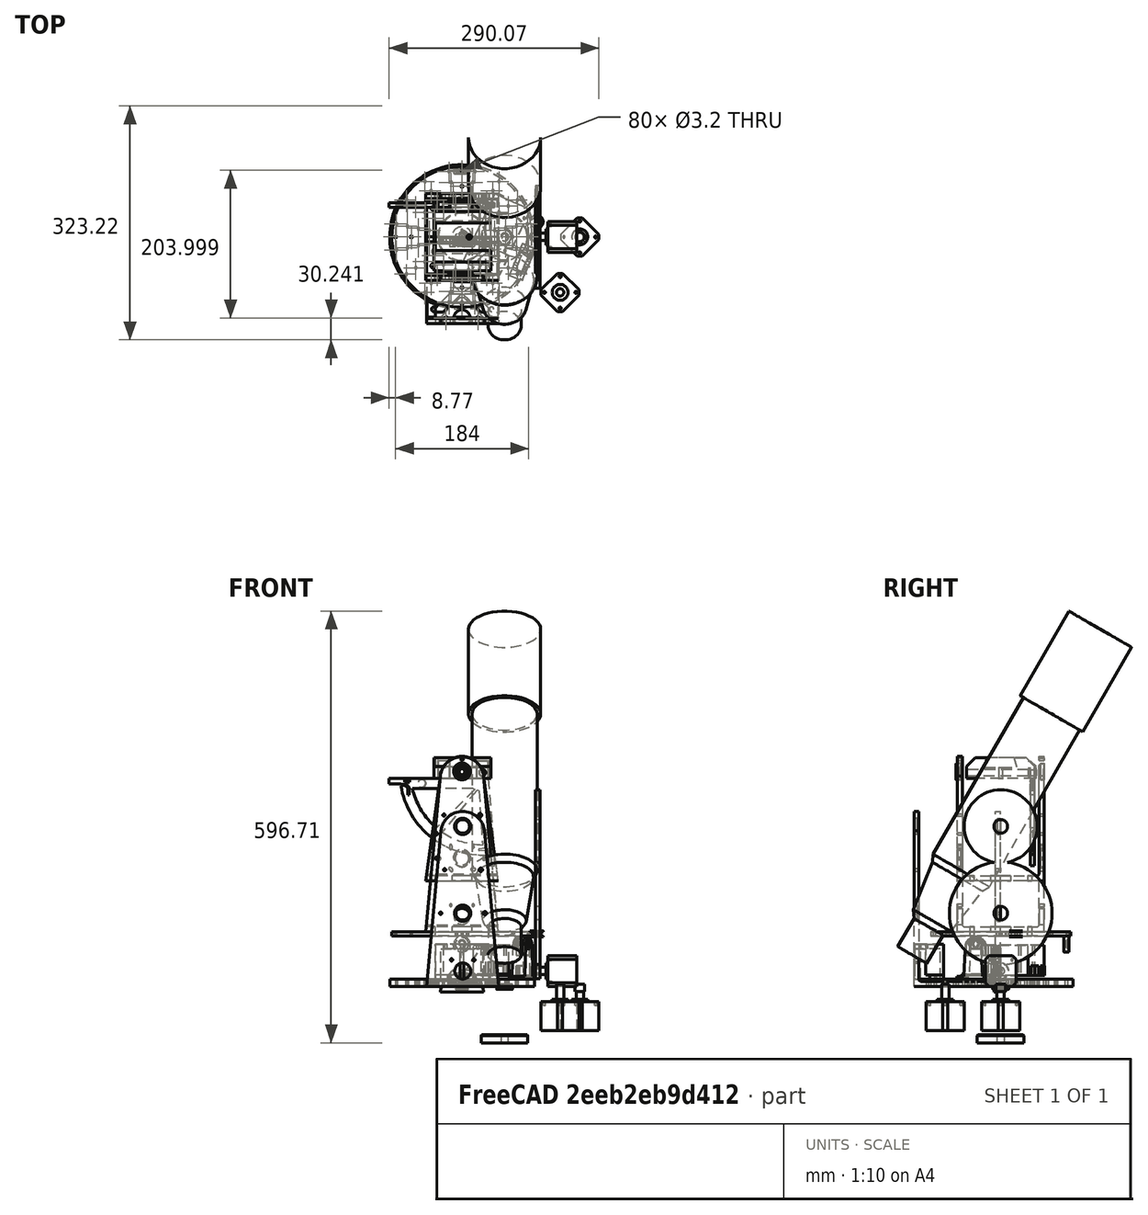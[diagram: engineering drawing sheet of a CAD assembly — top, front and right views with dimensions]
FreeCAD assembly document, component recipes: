
FREECAD ASSEMBLY — COMPONENT RECIPES ("202207 BATS - Begines Astro Tracking System")

This assembly document has 31 components, labeled P0..P30 below (a component is one placed body or linked part). 31 of them carry a construction recipe — the FreeCAD feature program that regenerates the part from scratch, quoted from this document or its linked companion documents; the rest are supplied as boundary geometry only. No exploded tour is included for this assembly.
NOTE — this tour is split across 2 documents so each fits a 32k-token context. This is document 1: the component sections continue in the remaining 1 document, each repeating the header above.
COMPONENT P0 — recipe-attached ("TRIPODE", modeled in this document).
Construction recipe (the document's own serialized feature program — sketch geometry with constraints, then the solid features built on it; lengths are millimeters unless a unit is written):

FEATURE [Sketcher::SketchObject] Sketch
  FullyConstrained = true
  MapMode = 5
  Support = -> [XY_Plane]
  sketch-geometry (2):
    g0: Circle CenterX=0 CenterY=0 CenterZ=0 NormalX=0 NormalY=0 NormalZ=1 AngleXU=0 Radius=32.25
    g1: Circle CenterX=0 CenterY=0 CenterZ=0 NormalX=0 NormalY=0 NormalZ=1 AngleXU=0 Radius=5.15
  constraints (4):
    c: Coincident(g0,g-1)
    c: Radius(g0) = 32.25
    c: Coincident(g1,g0)
    c: Radius(g1) = 5.15
FEATURE [PartDesign::Pad] Pad
  Direction = (1,1,1)
  Length = 11
  Length2 = 100
  Profile = -> Sketch
  Type = 0
FEATURE [PartDesign::Chamfer] Chamfer004
  Angle = 45
  Base = -> Pad [Edge3]
  BaseFeature = -> Pad
  ChamferType = 0
  FlipDirection = false
  Size = 1
  Size2 = 1
  SupportTransform = false
FEATURE [PartDesign::Body] Body  label="TRIPODE"
  Group = -> [Sketch,Pad,Chamfer004]
  Origin = -> Origin
  Placement = pos=(58.8,-0.2,-78) rot=(0,0,1;0rad)
  Tip = -> Chamfer004
COMPONENT P1 — recipe-attached ("BASE", modeled in this document).
Construction recipe (the document's own serialized feature program — sketch geometry with constraints, then the solid features built on it; lengths are millimeters unless a unit is written):

FEATURE [Sketcher::SketchObject] Sketch006
  FullyConstrained = true
  MapMode = 5
  Support = -> [XY_Plane002]
  sketch-geometry (17):
    g0: Circle CenterX=0 CenterY=0 CenterZ=0 NormalX=0 NormalY=0 NormalZ=1 AngleXU=0 Radius=97.1
    g1: Circle CenterX=0 CenterY=0 CenterZ=0 NormalX=0 NormalY=0 NormalZ=1 AngleXU=0 Radius=6.35
    g2: Circle CenterX=-40 CenterY=40 CenterZ=0 NormalX=0 NormalY=0 NormalZ=1 AngleXU=0 Radius=3.15
    g3: Circle CenterX=40 CenterY=40 CenterZ=0 NormalX=0 NormalY=0 NormalZ=1 AngleXU=0 Radius=3.15
    g4: Circle CenterX=40 CenterY=-40 CenterZ=0 NormalX=0 NormalY=0 NormalZ=1 AngleXU=0 Radius=3.15
    g5: Circle CenterX=-40 CenterY=-40 CenterZ=0 NormalX=0 NormalY=0 NormalZ=1 AngleXU=0 Radius=3.15
    g6: Circle CenterX=0 CenterY=92 CenterZ=0 NormalX=0 NormalY=0 NormalZ=1 AngleXU=0 Radius=1.6
    g7: Circle CenterX=0 CenterY=70 CenterZ=0 NormalX=0 NormalY=0 NormalZ=1 AngleXU=0 Radius=1.6
    g8: Circle CenterX=70 CenterY=0 CenterZ=0 NormalX=0 NormalY=0 NormalZ=1 AngleXU=0 Radius=1.6
    g9: Circle CenterX=92 CenterY=0 CenterZ=0 NormalX=0 NormalY=0 NormalZ=1 AngleXU=0 Radius=1.6
    g10: Circle CenterX=0 CenterY=-70 CenterZ=0 NormalX=0 NormalY=0 NormalZ=1 AngleXU=0 Radius=1.6
    g11: Circle CenterX=0 CenterY=-92 CenterZ=0 NormalX=0 NormalY=0 NormalZ=1 AngleXU=0 Radius=1.6
    g12: Circle CenterX=-92 CenterY=0 CenterZ=0 NormalX=0 NormalY=0 NormalZ=1 AngleXU=0 Radius=1.6
    g13: Circle CenterX=-70 CenterY=0 CenterZ=0 NormalX=0 NormalY=0 NormalZ=1 AngleXU=0 Radius=1.6
    g14: Circle CenterX=0 CenterY=9 CenterZ=0 NormalX=0 NormalY=0 NormalZ=1 AngleXU=0 Radius=1.55
    g15: Circle CenterX=7.79423 CenterY=-4.5 CenterZ=0 NormalX=0 NormalY=0 NormalZ=1 AngleXU=0 Radius=1.55
    g16: Circle CenterX=-7.79423 CenterY=-4.5 CenterZ=0 NormalX=0 NormalY=0 NormalZ=1 AngleXU=0 Radius=1.55
  constraints (48):
    c: Coincident(g0,g-1)
    c: Radius(g0) = 97.1
    c: Coincident(g1,g0)
    c: Equal(g2,g3)
    c: Equal(g2,g4)
    c: Equal(g2,g5)
    c: Radius(g2) = 3.15
    c: Horizontal(g2,g3)
    c: Horizontal(g5,g4)
    c: Vertical(g2,g5)
    c: DistanceX(g2,g3) = 80
    c: Vertical(g3,g4)
    c: DistanceY(g5,g2) = 80
    c: Symmetric(g2,g4,g0)
    c: PointOnObject(g6,g-2)
    c: PointOnObject(g7,g-2)
    c: PointOnObject(g8,g-1)
    c: PointOnObject(g9,g-1)
    c: PointOnObject(g10,g-2)
    c: PointOnObject(g11,g-2)
    c: PointOnObject(g12,g-1)
    c: PointOnObject(g13,g-1)
    c: Equal(g9,g8)
    c: Equal(g9,g10)
    c: Equal(g9,g11)
    c: Equal(g9,g13)
    c: Equal(g9,g12)
    c: Equal(g9,g7)
    c: Equal(g9,g6)
    c: Radius(g9) = 1.6
    c: DistanceX(g12,g0) = 92
    c: DistanceX(g9) = 92
    c: DistanceY(g6) = 92
    c: DistanceY(g11) = -92
    c: DistanceY(g10) = -70
    c: DistanceX(g8) = 70
    c: DistanceX(g13) = -70
    c: DistanceY(g7) = 70
    c: Radius(g1) = 6.35
    c: PointOnObject(g14,g-2)
    c: Equal(g14,g16)
    c: Equal(g14,g15)
    c: Radius(g14) = 1.55
    c: Distance(g14,g0) = 9
    c: Distance(g0,g15) = 9
    c: Symmetric(g16,g15,g-2)
    c: Distance(g14,g16) = 15.5885
    c: Distance(g16,g15) = 15.5885
FEATURE [PartDesign::Pad] Pad002
  Direction = (1,1,1)
  Length = 6
  Length2 = 100
  Profile = -> Sketch006
  Type = 0
FEATURE [PartDesign::Chamfer] Chamfer
  Angle = 45
  Base = -> Pad002 [Edge5,Edge6]
  BaseFeature = -> Pad002
  ChamferType = 0
  FlipDirection = false
  Size = 0.4
  Size2 = 1
  SupportTransform = false
FEATURE [PartDesign::Body] Body002  label="BASE"
  Group = -> [Sketch006,Pad002,Chamfer]
  Origin = -> Origin002
  Placement = pos=(-6e-15,0,69.6) rot=(0,0,1;0rad)
  Tip = -> Chamfer
COMPONENT P2 — recipe-attached ("BEARING 22x8x7base", modeled in this document).
Construction recipe (the document's own serialized feature program — sketch geometry with constraints, then the solid features built on it; lengths are millimeters unless a unit is written):

FEATURE [Sketcher::SketchObject] Sketch009
  FullyConstrained = true
  MapMode = 5
  Support = -> [XY_Plane003]
  sketch-geometry (2):
    g0: Circle CenterX=0 CenterY=0 CenterZ=0 NormalX=0 NormalY=0 NormalZ=1 AngleXU=0 Radius=4
    g1: Circle CenterX=0 CenterY=0 CenterZ=0 NormalX=0 NormalY=0 NormalZ=1 AngleXU=0 Radius=11
  constraints (4):
    c: Coincident(g0,g-1)
    c: Coincident(g1,g0)
    c: Radius(g0) = 4
    c: Radius(g1) = 11
FEATURE [PartDesign::Pad] Pad003
  Direction = (1,1,1)
  Length = 7
  Length2 = 100
  Profile = -> Sketch009
  Type = 0
FEATURE [Sketcher::SketchObject] Sketch011
  FullyConstrained = true
  MapMode = 5
  Placement = pos=(0,0,7) rot=(0,0,1;0rad)
  Support = -> [Pad003]
  sketch-geometry (2):
    g0: Circle CenterX=0 CenterY=0 CenterZ=0 NormalX=0 NormalY=0 NormalZ=1 AngleXU=0 Radius=5.5
    g1: Circle CenterX=0 CenterY=0 CenterZ=0 NormalX=0 NormalY=0 NormalZ=1 AngleXU=0 Radius=5.6
  constraints (4):
    c: Coincident(g0,g-1)
    c: Coincident(g1,g0)
    c: Radius(g0) = 5.5
    c: Radius(g1) = 5.6
FEATURE [PartDesign::Pocket] Pocket004
  BaseFeature = -> Pad003
  Length = 3
  Length2 = 100
  Midplane = true
  Profile = -> Sketch011
  Reversed = true
  Type = 0
FEATURE [Sketcher::SketchObject] Sketch010
  FullyConstrained = true
  MapMode = 5
  Placement = pos=(0,0,0) rot=(1,0,0;3.14159rad)
  Support = -> [Pocket004]
  sketch-geometry (2):
    g0: Circle CenterX=0 CenterY=0 CenterZ=0 NormalX=0 NormalY=0 NormalZ=1 AngleXU=0 Radius=5.5
    g1: Circle CenterX=0 CenterY=0 CenterZ=0 NormalX=0 NormalY=0 NormalZ=1 AngleXU=0 Radius=5.6
  constraints (4):
    c: Coincident(g0,g-1)
    c: Coincident(g1,g0)
    c: Radius(g0) = 5.5
    c: Radius(g1) = 5.6
FEATURE [PartDesign::Pocket] Pocket007
  BaseFeature = -> Pocket004
  Length = 3
  Length2 = 100
  Profile = -> Sketch010
  Type = 0
FEATURE [Sketcher::SketchObject] Sketch008
  FullyConstrained = true
  MapMode = 5
  Placement = pos=(0,0,7) rot=(0,0,1;0rad)
  Support = -> [Pocket007]
  sketch-geometry (2):
    g0: Circle CenterX=0 CenterY=0 CenterZ=0 NormalX=0 NormalY=0 NormalZ=1 AngleXU=0 Radius=9
    g1: Circle CenterX=0 CenterY=0 CenterZ=0 NormalX=0 NormalY=0 NormalZ=1 AngleXU=0 Radius=9.1
  constraints (4):
    c: Coincident(g0,g-1)
    c: Coincident(g1,g0)
    c: Radius(g0) = 9
    c: Radius(g1) = 9.1
FEATURE [PartDesign::Pocket] Pocket006
  BaseFeature = -> Pocket007
  Length = 1
  Length2 = 100
  Profile = -> Sketch008
  Type = 0
FEATURE [Sketcher::SketchObject] Sketch007
  FullyConstrained = true
  MapMode = 5
  Placement = pos=(0,0,0) rot=(1,0,0;3.14159rad)
  Support = -> [Pocket006]
  sketch-geometry (2):
    g0: Circle CenterX=0 CenterY=0 CenterZ=0 NormalX=0 NormalY=0 NormalZ=1 AngleXU=0 Radius=9
    g1: Circle CenterX=0 CenterY=0 CenterZ=0 NormalX=0 NormalY=0 NormalZ=1 AngleXU=0 Radius=9.1
  constraints (4):
    c: Coincident(g0,g-1)
    c: Coincident(g1,g0)
    c: Radius(g0) = 9
    c: Radius(g1) = 9.1
FEATURE [PartDesign::Pocket] Pocket005
  BaseFeature = -> Pocket006
  Length = 1
  Length2 = 100
  Profile = -> Sketch007
  Type = 0
FEATURE [PartDesign::Fillet] Fillet001
  Base = -> Pocket005 [Edge2,Edge3]
  BaseFeature = -> Pocket005
  Radius = 0.2
  SupportTransform = false
FEATURE [PartDesign::Body] Body003  label="BEARING 22x8x7base"
  Group = -> [Sketch009,Pad003,Sketch011,Pocket004,Sketch010,Pocket007,Sketch008,Pocket006,Sketch007,Pocket005,Fillet001]
  Origin = -> Origin003
  Placement = pos=(59,0,-4) rot=(0,0,1;0rad)
  Tip = -> Fillet001
COMPONENT P3 — recipe-attached ("GEARS", modeled in this document).
Construction recipe (the document's own serialized feature program — sketch geometry with constraints, then the solid features built on it; lengths are millimeters unless a unit is written):

FEATURE [Sketcher::SketchObject] Sketch017
  FullyConstrained = true
  MapMode = 5
  Placement = pos=(0,0,0) rot=(0.57735,0.57735,0.57735;2.0944rad)
  Support = -> [YZ_Plane004]
  sketch-geometry (7):
    g0: ArcOfCircle CenterX=0 CenterY=221.15 CenterZ=0 NormalX=0 NormalY=0 NormalZ=1 AngleXU=0 Radius=50.5 StartAngle=4.89915 EndAngle=10.8088
    g1: ArcOfCircle CenterX=0 CenterY=21.15 CenterZ=0 NormalX=0 NormalY=0 NormalZ=1 AngleXU=0 Radius=10.5 StartAngle=2.07708 EndAngle=7.3477
    g2: ArcOfCircle CenterX=0 CenterY=101.15 CenterZ=0 NormalX=0 NormalY=0 NormalZ=1 AngleXU=0 Radius=71 StartAngle=4.78417 EndAngle=7.72153
    g3: ArcOfCircle CenterX=0 CenterY=101.15 CenterZ=0 NormalX=0 NormalY=0 NormalZ=1 AngleXU=0 Radius=71 StartAngle=1.70325 EndAngle=4.64061
    g4: Circle CenterX=0 CenterY=101.15 CenterZ=0 NormalX=0 NormalY=0 NormalZ=1 AngleXU=0 Radius=9.5
    g5: Circle CenterX=0 CenterY=221.15 CenterZ=0 NormalX=0 NormalY=0 NormalZ=1 AngleXU=0 Radius=9.5
    g6: Circle CenterX=0 CenterY=21.15 CenterZ=0 NormalX=0 NormalY=0 NormalZ=1 AngleXU=0 Radius=2.6
  constraints (21):
    c: Radius(g0) = 50.5
    c: Radius(g1) = 10.5
    c: Coincident(g2,g0)
    c: Coincident(g2,g1)
    c: Coincident(g3,g2)
    c: Coincident(g3,g0)
    c: Coincident(g3,g1)
    c: DistanceY(g0) = 221.15
    c: DistanceY(g2) = 101.15
    c: Radius(g2) = 71
    c: Radius(g3) = 71
    c: Coincident(g4,g2)
    c: Coincident(g5,g0)
    c: Radius(g4) = 9.5
    c: Radius(g5) = 9.5
    c: Coincident(g6,g1)
    c: Radius(g6) = 2.6
    c: DistanceY(g1) = 21.15
    c: PointOnObject(g1,g-2)
    c: PointOnObject(g2,g-2)
    c: PointOnObject(g0,g-2)
FEATURE [PartDesign::Pad] Pad011
  Direction = (1,1,1)
  Length = 6
  Length2 = 100
  Placement = pos=(0,0,0) rot=(0.57735,0.57735,0.57735;2.0944rad)
  Profile = -> Sketch017
  Type = 0
FEATURE [PartDesign::Body] Body004  label="GEARS"
  Group = -> [Sketch017,Pad011]
  Origin = -> Origin004
  Placement = pos=(101.8,0,0) rot=(0,0,1;0rad)
  Tip = -> Pad011
COMPONENT P4 — recipe-attached ("TELESCOPIO", modeled in this document).
Construction recipe (the document's own serialized feature program — sketch geometry with constraints, then the solid features built on it; lengths are millimeters unless a unit is written):

FEATURE [Sketcher::SketchObject] Sketch014
  FullyConstrained = true
  MapMode = 5
  Support = -> [XY_Plane005]
  sketch-geometry (10):
    g0: LineSegment StartX=0 StartY=0 StartZ=0 EndX=0 EndY=50 EndZ=0
    g1: LineSegment StartX=0 StartY=50 StartZ=0 EndX=135 EndY=50 EndZ=0
    g2: LineSegment StartX=135 StartY=50 StartZ=0 EndX=135 EndY=45 EndZ=0
    g3: LineSegment StartX=135 StartY=45 StartZ=0 EndX=385 EndY=45 EndZ=0
    g4: LineSegment StartX=385 StartY=45 StartZ=0 EndX=395 EndY=40 EndZ=0
    g5: LineSegment StartX=395 StartY=40 StartZ=0 EndX=465 EndY=30 EndZ=0
    g6: LineSegment StartX=465 StartY=30 StartZ=0 EndX=475 EndY=23 EndZ=0
    g7: LineSegment StartX=520 StartY=0 StartZ=0 EndX=0 EndY=0 EndZ=0
    g8: LineSegment StartX=475 StartY=23 StartZ=0 EndX=520 EndY=23 EndZ=0
    g9: LineSegment StartX=520 StartY=23 StartZ=0 EndX=520 EndY=0 EndZ=0
  constraints (29):
    c: Coincident(g0,g1)
    c: Horizontal(g1)
    c: Coincident(g1,g2)
    c: Coincident(g2,g3)
    c: Horizontal(g3)
    c: Coincident(g3,g4)
    c: Coincident(g4,g5)
    c: Coincident(g5,g6)
    c: Coincident(g7,g0)
    c: Horizontal(g7)
    c: Vertical(g0)
    c: DistanceY(g0,g0) = 50
    c: Vertical(g2)
    c: DistanceY(g0,g2) = 45
    c: DistanceX(g1,g1) = 135
    c: DistanceX(g3,g3) = 250
    c: DistanceX(g3,g5) = 80
    c: DistanceY(g-1,g4) = 40
    c: DistanceX(g3,g4) = 10
    c: DistanceY(g-1,g5) = 30
    c: Coincident(g6,g8)
    c: Horizontal(g8)
    c: Coincident(g8,g9)
    c: Coincident(g9,g7)
    c: DistanceY(g-1,g8) = 23
    c: DistanceX(g6,g6) = 10
    c: Vertical(g9)
    c: DistanceX(g8,g8) = 45
    c: Coincident(g-1,g0)
FEATURE [PartDesign::Revolution] Revolution
  Angle = 360
  Axis = (1,0,0)
  Base = (0,0,0)
  Profile = -> Sketch014
  ReferenceAxis = -> Sketch014 [H_Axis]
FEATURE [PartDesign::Body] Body005  label="TELESCOPIO"
  Group = -> [Sketch014,Revolution]
  Origin = -> Origin005
  Placement = pos=(58.8541,137.678,493.712) rot=(0.447214,0.447214,-0.774597;1.82348rad)
  Tip = -> Revolution
COMPONENT P5 — recipe-attached ("NEMA17", modeled in this document).
Construction recipe (the document's own serialized feature program — sketch geometry with constraints, then the solid features built on it; lengths are millimeters unless a unit is written):

FEATURE [Sketcher::SketchObject] Sketch018
  FullyConstrained = true
  MapMode = 5
  Support = -> [XY_Plane006]
  sketch-geometry (4):
    g0: LineSegment StartX=-21.15 StartY=21.15 StartZ=0 EndX=21.15 EndY=21.15 EndZ=0
    g1: LineSegment StartX=21.15 StartY=21.15 StartZ=0 EndX=21.15 EndY=-21.15 EndZ=0
    g2: LineSegment StartX=21.15 StartY=-21.15 StartZ=0 EndX=-21.15 EndY=-21.15 EndZ=0
    g3: LineSegment StartX=-21.15 StartY=-21.15 StartZ=0 EndX=-21.15 EndY=21.15 EndZ=0
  constraints (11):
    c: Coincident(g0,g1)
    c: Coincident(g1,g2)
    c: Coincident(g2,g3)
    c: Coincident(g3,g0)
    c: Horizontal(g0)
    c: Horizontal(g2)
    c: Vertical(g1)
    c: Vertical(g3)
    c: DistanceX(g0,g0) = 42.3
    c: DistanceY(g1,g1) = 42.3
    c: Symmetric(g0,g1,g-1)
FEATURE [PartDesign::Pad] Pad005
  Direction = (1,1,1)
  Length = 40
  Length2 = 100
  Profile = -> Sketch018
  Type = 0
FEATURE [Sketcher::SketchObject] Sketch019
  FullyConstrained = true
  MapMode = 5
  Placement = pos=(0,0,40) rot=(0,0,1;0rad)
  Support = -> [Pad005]
  sketch-geometry (1):
    g0: Circle CenterX=0 CenterY=0 CenterZ=0 NormalX=0 NormalY=0 NormalZ=1 AngleXU=0 Radius=11
  constraints (2):
    c: Coincident(g0,g-1)
    c: Radius(g0) = 11
FEATURE [PartDesign::Pad] Pad006
  BaseFeature = -> Pad005
  Direction = (1,1,1)
  Length = 3
  Length2 = 100
  Profile = -> Sketch019
  Type = 0
FEATURE [Sketcher::SketchObject] Sketch020
  FullyConstrained = true
  MapMode = 5
  Placement = pos=(0,0,43) rot=(0,0,1;0rad)
  Support = -> [Pad006]
  sketch-geometry (1):
    g0: Circle CenterX=0 CenterY=0 CenterZ=0 NormalX=0 NormalY=0 NormalZ=1 AngleXU=0 Radius=5.1
  constraints (2):
    c: Coincident(g0,g-1)
    c: Radius(g0) = 5.1
FEATURE [PartDesign::Pad] Pad007
  BaseFeature = -> Pad006
  Direction = (1,1,1)
  Length = 21
  Length2 = 100
  Profile = -> Sketch020
  Type = 0
FEATURE [Sketcher::SketchObject] Sketch021
  FullyConstrained = true
  MapMode = 5
  Placement = pos=(0,0,0) rot=(1,0,0;3.14159rad)
  Support = -> [Pad007]
FEATURE [Sketcher::SketchObject] Sketch022
  ExternalGeometry = -> [Pad007]
  FullyConstrained = true
  MapMode = 5
  Placement = pos=(0,0,40) rot=(0,0,1;0rad)
  Support = -> [Pad007]
  sketch-geometry (4):
    g0: Circle CenterX=-15.5 CenterY=15.5 CenterZ=0 NormalX=0 NormalY=0 NormalZ=1 AngleXU=0 Radius=1.5
    g1: Circle CenterX=15.5 CenterY=15.5 CenterZ=0 NormalX=0 NormalY=0 NormalZ=1 AngleXU=0 Radius=1.5
    g2: Circle CenterX=15.5 CenterY=-15.5 CenterZ=0 NormalX=0 NormalY=0 NormalZ=1 AngleXU=0 Radius=1.5
    g3: Circle CenterX=-15.5 CenterY=-15.5 CenterZ=0 NormalX=0 NormalY=0 NormalZ=1 AngleXU=0 Radius=1.5
  constraints (14):
    c: Equal(g0,g1)
    c: Equal(g0,g2)
    c: Equal(g0,g3)
    c: Radius(g0) = 1.5
    c: Horizontal(g0,g1)
    c: Horizontal(g3,g2)
    c: Vertical(g0,g3)
    c: Vertical(g2,g1)
    c: DistanceX(g0,g1) = 31
    c: DistanceY(g3,g0) = 31
    c: DistanceX(g-5,g0) = 5.65
    c: DistanceY(g0,g-5) = 5.65
    c: DistanceX(g1,g-5) = 5.65
    c: DistanceY(g-6,g2) = 5.65
FEATURE [PartDesign::Pocket] Pocket011
  BaseFeature = -> Pad007
  Length = 5
  Length2 = 100
  Profile = -> Sketch022
  Type = 0
FEATURE [PartDesign::Chamfer] Chamfer001
  Angle = 45
  Base = -> Pocket011 [Edge2,Edge8,Edge1,Edge5]
  BaseFeature = -> Pocket011
  ChamferType = 0
  FlipDirection = false
  Size = 5
  Size2 = 1
  SupportTransform = false
FEATURE [PartDesign::Body] Body006  label="NEMA17"
  Group = -> [Sketch018,Pad005,Sketch019,Pad006,Sketch020,Pad007,Sketch021,Sketch022,Pocket011,Chamfer001]
  Origin = -> Origin006
  Placement = pos=(135.74,-76.6447,-61.1) rot=(0,0,-1;0.785398rad)
  Tip = -> Chamfer001
COMPONENT P6 — recipe-attached ("NEMA017-A", modeled in this document).
Construction recipe (the document's own serialized feature program — sketch geometry with constraints, then the solid features built on it; lengths are millimeters unless a unit is written):

FEATURE [Sketcher::SketchObject] Sketch026
  FullyConstrained = true
  MapMode = 5
  Support = -> [XY_Plane007]
  sketch-geometry (4):
    g0: LineSegment StartX=-21.15 StartY=21.15 StartZ=0 EndX=21.15 EndY=21.15 EndZ=0
    g1: LineSegment StartX=21.15 StartY=21.15 StartZ=0 EndX=21.15 EndY=-21.15 EndZ=0
    g2: LineSegment StartX=21.15 StartY=-21.15 StartZ=0 EndX=-21.15 EndY=-21.15 EndZ=0
    g3: LineSegment StartX=-21.15 StartY=-21.15 StartZ=0 EndX=-21.15 EndY=21.15 EndZ=0
  constraints (11):
    c: Coincident(g0,g1)
    c: Coincident(g1,g2)
    c: Coincident(g2,g3)
    c: Coincident(g3,g0)
    c: Horizontal(g0)
    c: Horizontal(g2)
    c: Vertical(g1)
    c: Vertical(g3)
    c: DistanceX(g0,g0) = 42.3
    c: DistanceY(g1,g1) = 42.3
    c: Symmetric(g0,g1,g-1)
FEATURE [PartDesign::Pad] Pad008
  Direction = (1,1,1)
  Length = 40
  Length2 = 100
  Profile = -> Sketch026
  Type = 0
FEATURE [Sketcher::SketchObject] Sketch025
  FullyConstrained = true
  MapMode = 5
  Placement = pos=(0,0,40) rot=(0,0,1;0rad)
  Support = -> [Pad008]
  sketch-geometry (1):
    g0: Circle CenterX=0 CenterY=0 CenterZ=0 NormalX=0 NormalY=0 NormalZ=1 AngleXU=0 Radius=11
  constraints (2):
    c: Coincident(g0,g-1)
    c: Radius(g0) = 11
FEATURE [PartDesign::Pad] Pad009
  BaseFeature = -> Pad008
  Direction = (1,1,1)
  Length = 3
  Length2 = 100
  Profile = -> Sketch025
  Type = 0
FEATURE [Sketcher::SketchObject] Sketch023
  FullyConstrained = true
  MapMode = 5
  Placement = pos=(0,0,43) rot=(0,0,1;0rad)
  Support = -> [Pad009]
  sketch-geometry (1):
    g0: Circle CenterX=0 CenterY=0 CenterZ=0 NormalX=0 NormalY=0 NormalZ=1 AngleXU=0 Radius=5.1
  constraints (2):
    c: Coincident(g0,g-1)
    c: Radius(g0) = 5.1
FEATURE [PartDesign::Pad] Pad010
  BaseFeature = -> Pad009
  Direction = (1,1,1)
  Length = 21
  Length2 = 100
  Profile = -> Sketch023
  Type = 0
FEATURE [Sketcher::SketchObject] Sketch024
  FullyConstrained = true
  MapMode = 5
  Placement = pos=(0,0,0) rot=(1,0,0;3.14159rad)
  Support = -> [Pad010]
FEATURE [Sketcher::SketchObject] Sketch027
  ExternalGeometry = -> [Pad010]
  FullyConstrained = true
  MapMode = 5
  Placement = pos=(0,0,40) rot=(0,0,1;0rad)
  Support = -> [Pad010]
  sketch-geometry (4):
    g0: Circle CenterX=-15.5 CenterY=15.5 CenterZ=0 NormalX=0 NormalY=0 NormalZ=1 AngleXU=0 Radius=1.5
    g1: Circle CenterX=15.5 CenterY=15.5 CenterZ=0 NormalX=0 NormalY=0 NormalZ=1 AngleXU=0 Radius=1.5
    g2: Circle CenterX=15.5 CenterY=-15.5 CenterZ=0 NormalX=0 NormalY=0 NormalZ=1 AngleXU=0 Radius=1.5
    g3: Circle CenterX=-15.5 CenterY=-15.5 CenterZ=0 NormalX=0 NormalY=0 NormalZ=1 AngleXU=0 Radius=1.5
  constraints (14):
    c: Equal(g0,g1)
    c: Equal(g0,g2)
    c: Equal(g0,g3)
    c: Radius(g0) = 1.5
    c: Horizontal(g0,g1)
    c: Horizontal(g3,g2)
    c: Vertical(g0,g3)
    c: Vertical(g2,g1)
    c: DistanceX(g0,g1) = 31
    c: DistanceY(g3,g0) = 31
    c: DistanceX(g-5,g0) = 5.65
    c: DistanceY(g0,g-5) = 5.65
    c: DistanceX(g1,g-5) = 5.65
    c: DistanceY(g-6,g2) = 5.65
FEATURE [PartDesign::Pocket] Pocket012
  BaseFeature = -> Pad010
  Length = 5
  Length2 = 100
  Profile = -> Sketch027
  Type = 0
FEATURE [PartDesign::Chamfer] Chamfer002
  Angle = 45
  Base = -> Pocket012 [Edge2,Edge8,Edge1,Edge5]
  BaseFeature = -> Pocket012
  ChamferType = 0
  FlipDirection = false
  Size = 5
  Size2 = 1
  SupportTransform = false
FEATURE [PartDesign::Body] Body007  label="NEMA017-A"
  Group = -> [Sketch026,Pad008,Sketch025,Pad009,Sketch023,Pad010,Sketch024,Sketch027,Pocket012,Chamfer002]
  Origin = -> Origin007
  Placement = pos=(159,0.1,21.25) rot=(0,-1,0;1.5708rad)
  Tip = -> Chamfer002
COMPONENT P7 — recipe-attached ("MEGA", modeled in this document).
Construction recipe (the document's own serialized feature program — sketch geometry with constraints, then the solid features built on it; lengths are millimeters unless a unit is written):

FEATURE [Sketcher::SketchObject] Sketch056
  FullyConstrained = true
  MapMode = 5
  Support = -> [XY_Plane013]
  sketch-geometry (17):
    g0: LineSegment StartX=-101.6 StartY=53.34 StartZ=0 EndX=-2.54 EndY=53.34 EndZ=0
    g1: LineSegment StartX=-2.54 StartY=53.34 StartZ=0 EndX=0 EndY=50.8 EndZ=0
    g2: LineSegment StartX=0 StartY=50.8 StartZ=0 EndX=0 EndY=40.64 EndZ=0
    g3: LineSegment StartX=0 StartY=40.64 StartZ=0 EndX=2.54 EndY=38.1 EndZ=0
    g4: LineSegment StartX=2.54 StartY=38.1 StartZ=0 EndX=2.54 EndY=3.81 EndZ=0
    g5: LineSegment StartX=2.54 StartY=3.81 StartZ=0 EndX=2.84e-14 EndY=1.27 EndZ=0
    g6: LineSegment StartX=2.84e-14 StartY=1.27 StartZ=0 EndX=2.84e-14 EndY=0 EndZ=0
    g7: LineSegment StartX=2.84e-14 StartY=0 StartZ=0 EndX=-101.6 EndY=0 EndZ=0
    g8: LineSegment StartX=-101.6 StartY=0 StartZ=0 EndX=-101.6 EndY=3.175 EndZ=0
    g9: LineSegment StartX=-101.6 StartY=3.175 StartZ=0 EndX=-103.505 EndY=3.175 EndZ=0
    g10: LineSegment StartX=-103.505 StartY=3.175 StartZ=0 EndX=-103.505 EndY=12.065 EndZ=0
    g11: LineSegment StartX=-103.505 StartY=12.065 StartZ=0 EndX=-101.6 EndY=12.065 EndZ=0
    g12: LineSegment StartX=-101.6 StartY=12.065 StartZ=0 EndX=-101.6 EndY=32.385 EndZ=0
    g13: LineSegment StartX=-101.6 StartY=32.385 StartZ=0 EndX=-107.95 EndY=32.385 EndZ=0
    g14: LineSegment StartX=-107.95 StartY=32.385 StartZ=0 EndX=-107.95 EndY=43.815 EndZ=0
    g15: LineSegment StartX=-107.95 StartY=43.815 StartZ=0 EndX=-101.6 EndY=43.815 EndZ=0
    g16: LineSegment StartX=-101.6 StartY=43.815 StartZ=0 EndX=-101.6 EndY=53.34 EndZ=0
  constraints (53):
    c: Horizontal(g0)
    c: Coincident(g0,g1)
    c: Coincident(g1,g2)
    c: Vertical(g2)
    c: Coincident(g2,g3)
    c: Coincident(g3,g4)
    c: Vertical(g4)
    c: Coincident(g4,g5)
    c: Coincident(g5,g6)
    c: Vertical(g6)
    c: Coincident(g6,g7)
    c: Horizontal(g7)
    c: Coincident(g7,g8)
    c: Vertical(g8)
    c: Coincident(g8,g9)
    c: Horizontal(g9)
    c: Coincident(g9,g10)
    c: Vertical(g10)
    c: Coincident(g10,g11)
    c: Horizontal(g11)
    c: Coincident(g11,g12)
    c: Coincident(g12,g13)
    c: Horizontal(g13)
    c: Coincident(g13,g14)
    c: Vertical(g14)
    c: Coincident(g14,g15)
    c: Horizontal(g15)
    c: Coincident(g15,g16)
    c: Coincident(g16,g0)
    c: DistanceX(g15,g15) = 6.35
    c: DistanceX(g9,g9) = 1.905
    c: Vertical(g8,g11)
    c: Vertical(g11,g12)
    c: Vertical(g12,g15)
    c: Vertical(g15,g0)
    c: DistanceX(g0,g1) = 2.54
    c: DistanceY(g1,g0) = 2.54
    c: DistanceY(g2,g2) = 10.16
    c: DistanceY(g3,g2) = 2.54
    c: DistanceX(g3,g3) = 2.54
    c: DistanceY(g5,g5) = 2.54
    c: DistanceX(g5,g5) = 2.54
    c: DistanceX(g7,g4) = 104.14
    c: DistanceY(g7,g0) = 53.34
    c: DistanceY(g8,g8) = 3.175
    c: DistanceY(g10,g10) = 8.89
    c: DistanceY(g12,g12) = 20.32
    c: DistanceY(g14,g14) = 11.43
    c: DistanceY(g16,g16) = 9.525
    c: DistanceY(g6,g6) = 1.27
    c: DistanceY(g4,g4) = 34.29
    c: PointOnObject(g6,g-1)
    c: DistanceX(g6) = 0
FEATURE [PartDesign::Pad] Pad017
  Direction = (1,1,1)
  Length = 2
  Length2 = 100
  Profile = -> Sketch056
  Type = 0
FEATURE [Sketcher::SketchObject] Sketch057
  ExternalGeometry = -> [Pad017]
  FullyConstrained = true
  MapMode = 5
  Placement = pos=(0,0,2) rot=(0,0,1;0rad)
  Support = -> [Pad017]
  sketch-geometry (4):
    g0: LineSegment StartX=-101.6 StartY=53.34 StartZ=0 EndX=-31.6 EndY=53.34 EndZ=0
    g1: LineSegment StartX=-31.6 StartY=53.34 StartZ=0 EndX=-31.6 EndY=0 EndZ=0
    g2: LineSegment StartX=-31.6 StartY=0 StartZ=0 EndX=-101.6 EndY=0 EndZ=0
    g3: LineSegment StartX=-101.6 StartY=0 StartZ=0 EndX=-101.6 EndY=53.34 EndZ=0
  constraints (11):
    c: Coincident(g0,g1)
    c: Coincident(g1,g2)
    c: Coincident(g2,g3)
    c: Coincident(g3,g0)
    c: Horizontal(g0)
    c: Horizontal(g2)
    c: Vertical(g1)
    c: Vertical(g3)
    c: Coincident(g0,g-8)
    c: PointOnObject(g1,g-9)
    c: DistanceX(g0,g0) = 70
FEATURE [PartDesign::Pad] Pad018
  BaseFeature = -> Pad017
  Direction = (1,1,1)
  Length = 40
  Length2 = 29
  Offset = 11
  Profile = -> Sketch057
  Type = 0
FEATURE [Sketcher::SketchObject] Sketch058
  ExternalGeometry = -> [Pad018]
  FullyConstrained = true
  MapMode = 5
  Placement = pos=(0,0,2) rot=(0,0,1;0rad)
  Support = -> [Pad018]
  sketch-geometry (8):
    g0: LineSegment StartX=-107.95 StartY=43.815 StartZ=0 EndX=-90.95 EndY=43.815 EndZ=0
    g1: LineSegment StartX=-90.95 StartY=43.815 StartZ=0 EndX=-90.95 EndY=32.385 EndZ=0
    g2: LineSegment StartX=-90.95 StartY=32.385 StartZ=0 EndX=-107.95 EndY=32.385 EndZ=0
    g3: LineSegment StartX=-107.95 StartY=32.385 StartZ=0 EndX=-107.95 EndY=43.815 EndZ=0
    g4: LineSegment StartX=-103.505 StartY=12.065 StartZ=0 EndX=-90.505 EndY=12.065 EndZ=0
    g5: LineSegment StartX=-90.505 StartY=12.065 StartZ=0 EndX=-90.505 EndY=3.175 EndZ=0
    g6: LineSegment StartX=-90.505 StartY=3.175 StartZ=0 EndX=-103.505 EndY=3.175 EndZ=0
    g7: LineSegment StartX=-103.505 StartY=3.175 StartZ=0 EndX=-103.505 EndY=12.065 EndZ=0
  constraints (20):
    c: Coincident(g0,g1)
    c: Coincident(g1,g2)
    c: Coincident(g2,g3)
    c: Coincident(g3,g0)
    c: Horizontal(g0)
    c: Horizontal(g2)
    c: Vertical(g1)
    c: Coincident(g0,g-3)
    c: Coincident(g-3,g2)
    c: DistanceX(g0,g0) = 17
    c: Coincident(g4,g5)
    c: Coincident(g5,g6)
    c: Coincident(g6,g7)
    c: Coincident(g7,g4)
    c: Horizontal(g4)
    c: Horizontal(g6)
    c: Vertical(g5)
    c: Coincident(g4,g-4)
    c: Coincident(g-4,g6)
    c: DistanceX(g4,g4) = 13
FEATURE [PartDesign::Pad] Pad019
  BaseFeature = -> Pad018
  Direction = (1,1,1)
  Length = 11
  Length2 = 100
  Profile = -> Sketch058
  Type = 0
FEATURE [Sketcher::SketchObject] Sketch059
  ExternalGeometry = -> [Pad019]
  FullyConstrained = true
  MapMode = 5
  Placement = pos=(0,0,0) rot=(1,0,0;3.14159rad)
  Support = -> [Pad019]
  sketch-geometry (6):
    g0: Circle CenterX=-86.36 CenterY=-2.54 CenterZ=0 NormalX=0 NormalY=0 NormalZ=1 AngleXU=0 Radius=1.5875
    g1: Circle CenterX=-11.43 CenterY=-2.54 CenterZ=0 NormalX=0 NormalY=0 NormalZ=1 AngleXU=0 Radius=1.5875
    g2: Circle CenterX=-87.63 CenterY=-50.8 CenterZ=0 NormalX=0 NormalY=0 NormalZ=1 AngleXU=0 Radius=1.5875
    g3: Circle CenterX=-5.08 CenterY=-50.8 CenterZ=0 NormalX=0 NormalY=0 NormalZ=1 AngleXU=0 Radius=1.5875
    g4: Circle CenterX=-35.56 CenterY=-17.78 CenterZ=0 NormalX=0 NormalY=0 NormalZ=1 AngleXU=0 Radius=1.5875
    g5: Circle CenterX=-35.56 CenterY=-45.72 CenterZ=0 NormalX=0 NormalY=0 NormalZ=1 AngleXU=0 Radius=1.5875
  constraints (18):
    c: Equal(g0,g2)
    c: Equal(g0,g1)
    c: Equal(g0,g3)
    c: Radius(g0) = 1.5875
    c: Horizontal(g0,g1)
    c: DistanceX(g-3,g0) = 15.24
    c: DistanceY(g0) = -2.54
    c: DistanceX(g-3,g1) = 90.17
    c: DistanceY(g-4,g2) = 2.54
    c: Horizontal(g3,g2)
    c: DistanceX(g-4,g2) = 13.97
    c: DistanceX(g-4,g3) = 96.52
    c: Equal(g4,g5)
    c: Radius(g4) = 1.5875
    c: Vertical(g4,g5)
    c: DistanceX(g-4,g5) = 66.04
    c: DistanceY(g-4,g5) = 7.62
    c: DistanceY(g-4,g4) = 35.56
FEATURE [PartDesign::Pocket] Pocket
  BaseFeature = -> Pad019
  Length = 50
  Length2 = 100
  Profile = -> Sketch059
  Type = 0
FEATURE [PartDesign::Body] Body012  label="MEGA"
  Group = -> [Sketch056,Pad017,Sketch057,Pad018,Sketch058,Pad019,Sketch059,Pocket]
  Origin = -> Origin012
  Placement = pos=(2.75616,-32.0303,15.15) rot=(0,0,-1;2.00713rad)
  Tip = -> Pocket
COMPONENT P8 — recipe-attached ("NEMA017-coronado", modeled in this document).
Construction recipe (the document's own serialized feature program — sketch geometry with constraints, then the solid features built on it; lengths are millimeters unless a unit is written):

FEATURE [Sketcher::SketchObject] Sketch076
  FullyConstrained = true
  MapMode = 5
  Support = -> [XY_Plane018]
  sketch-geometry (4):
    g0: LineSegment StartX=-21.15 StartY=21.15 StartZ=0 EndX=21.15 EndY=21.15 EndZ=0
    g1: LineSegment StartX=21.15 StartY=21.15 StartZ=0 EndX=21.15 EndY=-21.15 EndZ=0
    g2: LineSegment StartX=21.15 StartY=-21.15 StartZ=0 EndX=-21.15 EndY=-21.15 EndZ=0
    g3: LineSegment StartX=-21.15 StartY=-21.15 StartZ=0 EndX=-21.15 EndY=21.15 EndZ=0
  constraints (11):
    c: Coincident(g0,g1)
    c: Coincident(g1,g2)
    c: Coincident(g2,g3)
    c: Coincident(g3,g0)
    c: Horizontal(g0)
    c: Horizontal(g2)
    c: Vertical(g1)
    c: Vertical(g3)
    c: DistanceX(g0,g0) = 42.3
    c: DistanceY(g1,g1) = 42.3
    c: Symmetric(g0,g1,g-1)
FEATURE [PartDesign::Pad] Pad024
  Direction = (1,1,1)
  Length = 40
  Length2 = 100
  Profile = -> Sketch076
  Type = 0
FEATURE [Sketcher::SketchObject] Sketch075
  FullyConstrained = true
  MapMode = 5
  Placement = pos=(0,0,40) rot=(0,0,1;0rad)
  Support = -> [Pad024]
  sketch-geometry (1):
    g0: Circle CenterX=0 CenterY=0 CenterZ=0 NormalX=0 NormalY=0 NormalZ=1 AngleXU=0 Radius=11
  constraints (2):
    c: Coincident(g0,g-1)
    c: Radius(g0) = 11
FEATURE [PartDesign::Pad] Pad025
  BaseFeature = -> Pad024
  Direction = (1,1,1)
  Length = 3
  Length2 = 100
  Profile = -> Sketch075
  Type = 0
FEATURE [Sketcher::SketchObject] Sketch077
  FullyConstrained = true
  MapMode = 5
  Placement = pos=(0,0,43) rot=(0,0,1;0rad)
  Support = -> [Pad025]
  sketch-geometry (1):
    g0: Circle CenterX=0 CenterY=0 CenterZ=0 NormalX=0 NormalY=0 NormalZ=1 AngleXU=0 Radius=5.1
  constraints (2):
    c: Coincident(g0,g-1)
    c: Radius(g0) = 5.1
FEATURE [PartDesign::Pad] Pad026
  BaseFeature = -> Pad025
  Direction = (1,1,1)
  Length = 21
  Length2 = 100
  Profile = -> Sketch077
  Type = 0
FEATURE [Sketcher::SketchObject] Sketch078
  FullyConstrained = true
  MapMode = 5
  Placement = pos=(0,0,0) rot=(1,0,0;3.14159rad)
  Support = -> [Pad026]
FEATURE [Sketcher::SketchObject] Sketch079
  ExternalGeometry = -> [Pad026]
  FullyConstrained = true
  MapMode = 5
  Placement = pos=(0,0,40) rot=(0,0,1;0rad)
  Support = -> [Pad026]
  sketch-geometry (4):
    g0: Circle CenterX=-15.5 CenterY=15.5 CenterZ=0 NormalX=0 NormalY=0 NormalZ=1 AngleXU=0 Radius=1.5
    g1: Circle CenterX=15.5 CenterY=15.5 CenterZ=0 NormalX=0 NormalY=0 NormalZ=1 AngleXU=0 Radius=1.5
    g2: Circle CenterX=15.5 CenterY=-15.5 CenterZ=0 NormalX=0 NormalY=0 NormalZ=1 AngleXU=0 Radius=1.5
    g3: Circle CenterX=-15.5 CenterY=-15.5 CenterZ=0 NormalX=0 NormalY=0 NormalZ=1 AngleXU=0 Radius=1.5
  constraints (14):
    c: Equal(g0,g1)
    c: Equal(g0,g2)
    c: Equal(g0,g3)
    c: Radius(g0) = 1.5
    c: Horizontal(g0,g1)
    c: Horizontal(g3,g2)
    c: Vertical(g0,g3)
    c: Vertical(g2,g1)
    c: DistanceX(g0,g1) = 31
    c: DistanceY(g3,g0) = 31
    c: DistanceX(g-5,g0) = 5.65
    c: DistanceY(g0,g-5) = 5.65
    c: DistanceX(g1,g-5) = 5.65
    c: DistanceY(g-6,g2) = 5.65
FEATURE [PartDesign::Pocket] Pocket047
  BaseFeature = -> Pad026
  Length = 5
  Length2 = 100
  Profile = -> Sketch079
  Type = 0
FEATURE [PartDesign::Chamfer] Chamfer008
  Angle = 45
  Base = -> Pocket047 [Edge2,Edge8,Edge1,Edge5]
  BaseFeature = -> Pocket047
  ChamferType = 0
  FlipDirection = false
  Size = 5
  Size2 = 1
  SupportTransform = false
FEATURE [Sketcher::SketchObject] Sketch080
  FullyConstrained = true
  MapMode = 5
  Placement = pos=(0,0,64) rot=(0,0,1;0rad)
  Support = -> [Chamfer008]
  sketch-geometry (1):
    g0: Circle CenterX=0 CenterY=0 CenterZ=0 NormalX=0 NormalY=0 NormalZ=1 AngleXU=0 Radius=6.75
  constraints (2):
    c: Coincident(g0,g-1)
    c: Radius(g0) = 6.75
FEATURE [PartDesign::Pad] Pad027
  BaseFeature = -> Chamfer008
  Direction = (1,1,1)
  Length = 10
  Length2 = 100
  Profile = -> Sketch080
  Reversed = true
  Type = 0
FEATURE [PartDesign::Body] Body017  label="NEMA017-coronado"
  Group = -> [Sketch076,Pad024,Sketch075,Pad025,Sketch077,Pad026,Sketch078,Sketch079,Pocket047,Chamfer008,Sketch080,Pad027]
  Origin = -> Origin017
  Placement = pos=(162.924,-0.0108408,-61.1) rot=(0,0,1;0.785398rad)
  Tip = -> Pad027
COMPONENT P9 — recipe-attached ("AGARRENEMA", modeled in this document).
Construction recipe (the document's own serialized feature program — sketch geometry with constraints, then the solid features built on it; lengths are millimeters unless a unit is written):

FEATURE [Sketcher::SketchObject] Sketch081
  FullyConstrained = false
  MapMode = 5
  Support = -> [XY_Plane019]
  sketch-geometry (12):
    g0: LineSegment StartX=133.079 StartY=18 StartZ=0 EndX=133.079 EndY=-18 EndZ=0
    g1: LineSegment StartX=133.079 StartY=-18 StartZ=0 EndX=151.918 EndY=-36.8396 EndZ=0
    g2: LineSegment StartX=151.918 StartY=-36.8396 StartZ=0 EndX=177.784 EndY=-36.8396 EndZ=0
    g3: LineSegment StartX=177.784 StartY=-36.8396 StartZ=0 EndX=177.784 EndY=36.8396 EndZ=0
    g4: LineSegment StartX=177.784 StartY=36.8396 StartZ=0 EndX=151.918 EndY=36.8396 EndZ=0
    g5: LineSegment StartX=151.918 StartY=36.8396 StartZ=0 EndX=133.079 EndY=18 EndZ=0
    g6: Circle CenterX=144.079 CenterY=0 CenterZ=0 NormalX=0 NormalY=0 NormalZ=1 AngleXU=0 Radius=1.6
    g7: Circle CenterX=165.999 CenterY=21.92 CenterZ=0 NormalX=0 NormalY=0 NormalZ=1 AngleXU=0 Radius=1.6
    g8: Circle CenterX=165.999 CenterY=-21.92 CenterZ=0 NormalX=0 NormalY=0 NormalZ=1 AngleXU=0 Radius=1.6
    g9: Circle CenterX=165.999 CenterY=1.1e-15 CenterZ=0 NormalX=0 NormalY=0 NormalZ=1 AngleXU=0 Radius=11.2
    g10: Circle CenterX=144.079 CenterY=18 CenterZ=0 NormalX=0 NormalY=0 NormalZ=1 AngleXU=0 Radius=1.6
    g11: Circle CenterX=144.079 CenterY=-18 CenterZ=0 NormalX=0 NormalY=0 NormalZ=1 AngleXU=0 Radius=1.6
  constraints (27):
    c: Coincident(g0,g1)
    c: Coincident(g1,g2)
    c: Horizontal(g2)
    c: Coincident(g2,g3)
    c: Coincident(g3,g4)
    c: Coincident(g4,g5)
    c: Coincident(g5,g0)
    c: Symmetric(g0,g0,g-1)
    c: Symmetric(g4,g1,g-1)
    c: Symmetric(g2,g3,g-1)
    c: PointOnObject(g6,g-1)
    c: Equal(g8,g7)
    c: Equal(g8,g6)
    c: Radius(g8) = 1.6
    c: Symmetric(g7,g8,g-1)
    c: Distance(g7,g6) = 31
    c: DistanceY(g8,g7) = 43.84
    c: DistanceX(g0,g6) = 11
    c: Angle(g1) = -0.785398
    c: Radius(g9) = 11.2
    c: Symmetric(g7,g8,g9)
    c: Equal(g11,g10)
    c: Radius(g11) = 1.6
    c: Symmetric(g10,g11,g6)
    c: Vertical(g10,g11)
    c: DistanceY(g11,g10) = 36
    c: DistanceY(g0,g0) = 36
FEATURE [PartDesign::Pad] Pad028
  Direction = (1,1,1)
  Length = 48
  Length2 = 100
  Profile = -> Sketch081
  Reversed = true
  Type = 0
FEATURE [Sketcher::SketchObject] Sketch082
  ExternalGeometry = -> [Pad028]
  FullyConstrained = true
  MapMode = 5
  Placement = pos=(0,0,-48) rot=(1,0,0;3.14159rad)
  Support = -> [Pad028]
  sketch-geometry (6):
    g0: LineSegment StartX=177.784 StartY=29.5 StartZ=0 EndX=164.784 EndY=29.5 EndZ=0
    g1: LineSegment StartX=164.784 StartY=-29.5 StartZ=0 EndX=177.784 EndY=-29.5 EndZ=0
    g2: LineSegment StartX=164.784 StartY=29.5 StartZ=0 EndX=137.784 EndY=2.5 EndZ=0
    g3: LineSegment StartX=137.784 StartY=2.5 StartZ=0 EndX=137.784 EndY=-2.5 EndZ=0
    g4: LineSegment StartX=137.784 StartY=-2.5 StartZ=0 EndX=164.784 EndY=-29.5 EndZ=0
    g5: LineSegment StartX=177.784 StartY=29.5 StartZ=0 EndX=177.784 EndY=-29.5 EndZ=0
  constraints (16):
    c: Horizontal(g0)
    c: Horizontal(g1)
    c: Coincident(g0,g2)
    c: Coincident(g2,g3)
    c: Coincident(g3,g4)
    c: Coincident(g4,g1)
    c: Symmetric(g2,g3,g-1)
    c: Angle(g2) = -2.35619
    c: Angle(g4) = -0.785398
    c: PointOnObject(g0,g-8)
    c: Symmetric(g0,g1,g-1)
    c: Coincident(g5,g0)
    c: Coincident(g5,g1)
    c: DistanceY(g5,g5) = 59
    c: DistanceX(g2,g0) = 27
    c: DistanceX(g0,g0) = 13
FEATURE [PartDesign::Pocket] Pocket048
  BaseFeature = -> Pad028
  Length = 42
  Length2 = 100
  Profile = -> Sketch082
  Type = 0
FEATURE [Sketcher::SketchObject] Sketch083
  ExternalGeometry = -> [Pocket048]
  FullyConstrained = true
  MapMode = 5
  Support = -> [Pocket048]
  sketch-geometry (7):
    g0: LineSegment StartX=157.918 StartY=26.18 StartZ=0 EndX=131.738 EndY=0 EndZ=0
    g1: LineSegment StartX=131.738 StartY=0 StartZ=0 EndX=157.918 EndY=-26.18 EndZ=0
    g2: LineSegment StartX=157.918 StartY=-26.18 StartZ=0 EndX=157.918 EndY=-40 EndZ=0
    g3: LineSegment StartX=157.918 StartY=40 StartZ=0 EndX=157.918 EndY=26.18 EndZ=0
    g4: LineSegment StartX=157.918 StartY=40 StartZ=0 EndX=107.918 EndY=40 EndZ=0
    g5: LineSegment StartX=107.918 StartY=40 StartZ=0 EndX=107.918 EndY=-40 EndZ=0
    g6: LineSegment StartX=107.918 StartY=-40 StartZ=0 EndX=157.918 EndY=-40 EndZ=0
  constraints (19):
    c: PointOnObject(g0,g-1)
    c: Coincident(g0,g1)
    c: Angle(g0) = -2.35619
    c: Symmetric(g0,g1,g-1)
    c: Coincident(g0,g3)
    c: Coincident(g1,g2)
    c: Coincident(g3,g4)
    c: Coincident(g4,g5)
    c: Coincident(g5,g6)
    c: Coincident(g6,g2)
    c: Vertical(g3)
    c: Vertical(g2)
    c: Symmetric(g4,g5,g-1)
    c: Horizontal(g6)
    c: Horizontal(g4)
    c: DistanceY(g2,g3) = 80
    c: DistanceX(g5,g2) = 50
    c: DistanceX(g-3,g0) = 6
    c: DistanceY(g0,g0) = 26.18
FEATURE [PartDesign::Pocket] Pocket049
  BaseFeature = -> Pocket048
  Length = 42
  Length2 = 100
  Profile = -> Sketch083
  Type = 0
FEATURE [Sketcher::SketchObject] Sketch084
  FullyConstrained = false
  MapMode = 5
  Support = -> [Pocket049]
  sketch-geometry (4):
    g0: LineSegment StartX=173.325 StartY=38.7531 StartZ=0 EndX=183.354 EndY=38.7531 EndZ=0
    g1: LineSegment StartX=183.354 StartY=38.7531 StartZ=0 EndX=183.354 EndY=-39.1093 EndZ=0
    g2: LineSegment StartX=183.354 StartY=-39.1093 StartZ=0 EndX=173.325 EndY=-39.1093 EndZ=0
    g3: LineSegment StartX=173.325 StartY=-39.1093 StartZ=0 EndX=173.325 EndY=38.7531 EndZ=0
  constraints (8):
    c: Coincident(g0,g1)
    c: Coincident(g1,g2)
    c: Coincident(g2,g3)
    c: Coincident(g3,g0)
    c: Horizontal(g0)
    c: Horizontal(g2)
    c: Vertical(g1)
    c: Vertical(g3)
FEATURE [PartDesign::Pocket] Pocket050
  BaseFeature = -> Pocket049
  Length = 48
  Length2 = 100
  Profile = -> Sketch084
  Type = 0
FEATURE [PartDesign::Body] Body018  label="AGARRENEMA"
  Group = -> [Sketch081,Pad028,Sketch082,Pocket048,Sketch083,Pocket049,Sketch084,Pocket050]
  Origin = -> Origin018
  Placement = pos=(1.55e-13,54,58) rot=(0,0,-1;1.5708rad)
  Tip = -> Pocket050
COMPONENT P10 — recipe-attached ("CARCASA", modeled in this document).
Construction recipe (the document's own serialized feature program — sketch geometry with constraints, then the solid features built on it; lengths are millimeters unless a unit is written):

FEATURE [Sketcher::SketchObject] Sketch085
  FullyConstrained = true
  MapMode = 5
  Support = -> [XY_Plane020]
  sketch-geometry (133):
    g0: LineSegment StartX=76.7155 StartY=-51.2597 StartZ=0 EndX=90.4921 EndY=-18 EndZ=0
    g1: LineSegment StartX=90.4921 StartY=-18 StartZ=0 EndX=90.4921 EndY=18 EndZ=0
    g2: LineSegment StartX=90.4921 StartY=18 StartZ=0 EndX=76.7155 EndY=51.2597 EndZ=0
    g3: LineSegment StartX=76.7155 StartY=51.2597 StartZ=0 EndX=51.2597 EndY=76.7155 EndZ=0
    g4: LineSegment StartX=51.2597 StartY=76.7155 StartZ=0 EndX=18 EndY=90.4921 EndZ=0
    g5: LineSegment StartX=18 StartY=90.4921 StartZ=0 EndX=-18 EndY=90.4921 EndZ=0
    g6: LineSegment StartX=-18 StartY=90.4921 StartZ=0 EndX=-51.2597 EndY=76.7155 EndZ=0
    g7: LineSegment StartX=-51.2597 StartY=76.7155 StartZ=0 EndX=-76.7155 EndY=51.2597 EndZ=0
    g8: LineSegment StartX=-76.7155 StartY=51.2597 StartZ=0 EndX=-90.4921 EndY=18 EndZ=0
    g9: LineSegment StartX=-90.4921 StartY=18 StartZ=0 EndX=-90.4921 EndY=-18 EndZ=0
    g10: LineSegment StartX=-90.4921 StartY=-18 StartZ=0 EndX=-76.7155 EndY=-51.2597 EndZ=0
    g11: LineSegment StartX=-76.7155 StartY=-51.2597 StartZ=0 EndX=-51.2597 EndY=-76.7155 EndZ=0
    g12: LineSegment StartX=-51.2597 StartY=-76.7155 StartZ=0 EndX=-18 EndY=-90.4921 EndZ=0
    g13: LineSegment StartX=-18 StartY=-90.4921 StartZ=0 EndX=18 EndY=-90.4921 EndZ=0
    g14: LineSegment StartX=18 StartY=-90.4921 StartZ=0 EndX=51.2597 EndY=-76.7155 EndZ=0
    g15: LineSegment StartX=51.2597 StartY=-76.7155 StartZ=0 EndX=76.7155 EndY=-51.2597 EndZ=0
    g16: Circle CenterX=0 CenterY=0 CenterZ=0 NormalX=0 NormalY=0 NormalZ=1 AngleXU=0 Radius=92.265
    g17: LineSegment StartX=51.1437 StartY=-34.1731 StartZ=0 EndX=60.3281 EndY=-12 EndZ=0
    g18: LineSegment StartX=60.3281 StartY=-12 StartZ=0 EndX=60.3281 EndY=12 EndZ=0
    g19: LineSegment StartX=60.3281 StartY=12 StartZ=0 EndX=51.1437 EndY=34.1731 EndZ=0
    g20: LineSegment StartX=51.1437 StartY=34.1731 StartZ=0 EndX=34.1731 EndY=51.1437 EndZ=0
    g21: LineSegment StartX=34.1731 StartY=51.1437 StartZ=0 EndX=12 EndY=60.3281 EndZ=0
    g22: LineSegment StartX=12 StartY=60.3281 StartZ=0 EndX=-12 EndY=60.3281 EndZ=0
    g23: LineSegment StartX=-12 StartY=60.3281 StartZ=0 EndX=-34.1731 EndY=51.1437 EndZ=0
    g24: LineSegment StartX=-34.1731 StartY=51.1437 StartZ=0 EndX=-51.1437 EndY=34.1731 EndZ=0
    g25: LineSegment StartX=-51.1437 StartY=34.1731 StartZ=0 EndX=-60.3281 EndY=12 EndZ=0
    g26: LineSegment StartX=-60.3281 StartY=12 StartZ=0 EndX=-60.3281 EndY=-12 EndZ=0
    g27: LineSegment StartX=-60.3281 StartY=-12 StartZ=0 EndX=-51.1437 EndY=-34.1731 EndZ=0
    g28: LineSegment StartX=-51.1437 StartY=-34.1731 StartZ=0 EndX=-34.1731 EndY=-51.1437 EndZ=0
    g29: LineSegment StartX=-34.1731 StartY=-51.1437 StartZ=0 EndX=-12 EndY=-60.3281 EndZ=0
    g30: LineSegment StartX=-12 StartY=-60.3281 StartZ=0 EndX=12 EndY=-60.3281 EndZ=0
    g31: LineSegment StartX=12 StartY=-60.3281 StartZ=0 EndX=34.1731 EndY=-51.1437 EndZ=0
    g32: LineSegment StartX=34.1731 StartY=-51.1437 StartZ=0 EndX=51.1437 EndY=-34.1731 EndZ=0
    g33: Circle CenterX=0 CenterY=0 CenterZ=0 NormalX=0 NormalY=0 NormalZ=1 AngleXU=0 Radius=61.51
    g34: LineSegment StartX=63.9296 StartY=-42.7164 StartZ=0 EndX=75.4101 EndY=-15 EndZ=0
    g35: LineSegment StartX=75.4101 StartY=-15 StartZ=0 EndX=75.4101 EndY=15 EndZ=0
    g36: LineSegment StartX=75.4101 StartY=15 StartZ=0 EndX=63.9296 EndY=42.7164 EndZ=0
    g37: LineSegment StartX=63.9296 StartY=42.7164 StartZ=0 EndX=42.7164 EndY=63.9296 EndZ=0
    g38: LineSegment StartX=42.7164 StartY=63.9296 StartZ=0 EndX=15 EndY=75.4101 EndZ=0
    g39: LineSegment StartX=15 StartY=75.4101 StartZ=0 EndX=-15 EndY=75.4101 EndZ=0
    g40: LineSegment StartX=-15 StartY=75.4101 StartZ=0 EndX=-42.7164 EndY=63.9296 EndZ=0
    g41: LineSegment StartX=-42.7164 StartY=63.9296 StartZ=0 EndX=-63.9296 EndY=42.7164 EndZ=0
    g42: LineSegment StartX=-63.9296 StartY=42.7164 StartZ=0 EndX=-75.4101 EndY=15 EndZ=0
    g43: LineSegment StartX=-75.4101 StartY=15 StartZ=0 EndX=-75.4101 EndY=-15 EndZ=0
    g44: LineSegment StartX=-75.4101 StartY=-15 StartZ=0 EndX=-63.9296 EndY=-42.7164 EndZ=0
    g45: LineSegment StartX=-63.9296 StartY=-42.7164 StartZ=0 EndX=-42.7164 EndY=-63.9296 EndZ=0
    g46: LineSegment StartX=-42.7164 StartY=-63.9296 StartZ=0 EndX=-15 EndY=-75.4101 EndZ=0
    g47: LineSegment StartX=-15 StartY=-75.4101 StartZ=0 EndX=15 EndY=-75.4101 EndZ=0
    g48: LineSegment StartX=15 StartY=-75.4101 StartZ=0 EndX=42.7164 EndY=-63.9296 EndZ=0
    g49: LineSegment StartX=42.7164 StartY=-63.9296 StartZ=0 EndX=63.9296 EndY=-42.7164 EndZ=0
    g50: Circle CenterX=0 CenterY=0 CenterZ=0 NormalX=0 NormalY=0 NormalZ=1 AngleXU=0 Radius=76.8875
    g51: LineSegment StartX=38.3578 StartY=-25.6298 StartZ=0 EndX=45.2461 EndY=-9 EndZ=0
    g52: LineSegment StartX=45.2461 StartY=-9 StartZ=0 EndX=45.2461 EndY=9 EndZ=0
    g53: LineSegment StartX=45.2461 StartY=9 StartZ=0 EndX=38.3578 EndY=25.6298 EndZ=0
    g54: LineSegment StartX=38.3578 StartY=25.6298 StartZ=0 EndX=25.6298 EndY=38.3578 EndZ=0
    g55: LineSegment StartX=25.6298 StartY=38.3578 StartZ=0 EndX=9 EndY=45.2461 EndZ=0
    g56: LineSegment StartX=9 StartY=45.2461 StartZ=0 EndX=-9 EndY=45.2461 EndZ=0
    g57: LineSegment StartX=-9 StartY=45.2461 StartZ=0 EndX=-25.6298 EndY=38.3578 EndZ=0
    g58: LineSegment StartX=-25.6298 StartY=38.3578 StartZ=0 EndX=-38.3578 EndY=25.6298 EndZ=0
    g59: LineSegment StartX=-38.3578 StartY=25.6298 StartZ=0 EndX=-45.2461 EndY=9 EndZ=0
    g60: LineSegment StartX=-45.2461 StartY=9 StartZ=0 EndX=-45.2461 EndY=-9 EndZ=0
    g61: LineSegment StartX=-45.2461 StartY=-9 StartZ=0 EndX=-38.3578 EndY=-25.6298 EndZ=0
    g62: LineSegment StartX=-38.3578 StartY=-25.6298 StartZ=0 EndX=-25.6298 EndY=-38.3578 EndZ=0
    g63: LineSegment StartX=-25.6298 StartY=-38.3578 StartZ=0 EndX=-9 EndY=-45.2461 EndZ=0
    g64: LineSegment StartX=-9 StartY=-45.2461 StartZ=0 EndX=9 EndY=-45.2461 EndZ=0
    g65: LineSegment StartX=9 StartY=-45.2461 StartZ=0 EndX=25.6298 EndY=-38.3578 EndZ=0
    g66: LineSegment StartX=25.6298 StartY=-38.3578 StartZ=0 EndX=38.3578 EndY=-25.6298 EndZ=0
    g67: Circle CenterX=0 CenterY=0 CenterZ=0 NormalX=0 NormalY=0 NormalZ=1 AngleXU=0 Radius=46.1325
    g68: Circle CenterX=-18 CenterY=90.4921 CenterZ=0 NormalX=0 NormalY=0 NormalZ=1 AngleXU=0 Radius=1.6
    g69: Circle CenterX=18 CenterY=90.4921 CenterZ=0 NormalX=0 NormalY=0 NormalZ=1 AngleXU=0 Radius=1.6
    g70: Circle CenterX=51.2597 CenterY=76.7155 CenterZ=0 NormalX=0 NormalY=0 NormalZ=1 AngleXU=0 Radius=1.6
    g71: Circle CenterX=76.7155 CenterY=51.2597 CenterZ=0 NormalX=0 NormalY=0 NormalZ=1 AngleXU=0 Radius=1.6
    g72: Circle CenterX=90.4921 CenterY=18 CenterZ=0 NormalX=0 NormalY=0 NormalZ=1 AngleXU=0 Radius=1.6
    g73: Circle CenterX=90.4921 CenterY=-18 CenterZ=0 NormalX=0 NormalY=0 NormalZ=1 AngleXU=0 Radius=1.6
    g74: Circle CenterX=76.7155 CenterY=-51.2597 CenterZ=0 NormalX=0 NormalY=0 NormalZ=1 AngleXU=0 Radius=1.6
    g75: Circle CenterX=51.2597 CenterY=-76.7155 CenterZ=0 NormalX=0 NormalY=0 NormalZ=1 AngleXU=0 Radius=1.6
    g76: Circle CenterX=18 CenterY=-90.4921 CenterZ=0 NormalX=0 NormalY=0 NormalZ=1 AngleXU=0 Radius=1.6
    g77: Circle CenterX=-18 CenterY=-90.4921 CenterZ=0 NormalX=0 NormalY=0 NormalZ=1 AngleXU=0 Radius=1.6
    g78: Circle CenterX=-51.2597 CenterY=-76.7155 CenterZ=0 NormalX=0 NormalY=0 NormalZ=1 AngleXU=0 Radius=1.6
    g79: Circle CenterX=-76.7155 CenterY=-51.2597 CenterZ=0 NormalX=0 NormalY=0 NormalZ=1 AngleXU=0 Radius=1.6
    g80: Circle CenterX=-90.4921 CenterY=-18 CenterZ=0 NormalX=0 NormalY=0 NormalZ=1 AngleXU=0 Radius=1.6
    g81: Circle CenterX=-90.4921 CenterY=18 CenterZ=0 NormalX=0 NormalY=0 NormalZ=1 AngleXU=0 Radius=1.6
    g82: Circle CenterX=-76.7155 CenterY=51.2597 CenterZ=0 NormalX=0 NormalY=0 NormalZ=1 AngleXU=0 Radius=1.6
    g83: Circle CenterX=-51.2597 CenterY=76.7155 CenterZ=0 NormalX=0 NormalY=0 NormalZ=1 AngleXU=0 Radius=1.6
    g84: Circle CenterX=0 CenterY=0 CenterZ=0 NormalX=0 NormalY=0 NormalZ=1 AngleXU=0 Radius=100
    g85: Circle CenterX=-75.4101 CenterY=15 CenterZ=0 NormalX=0 NormalY=0 NormalZ=1 AngleXU=0 Radius=1.6
    g86: Circle CenterX=-75.4101 CenterY=-15 CenterZ=0 NormalX=0 NormalY=0 NormalZ=1 AngleXU=0 Radius=1.6
    g87: Circle CenterX=-63.9296 CenterY=-42.7164 CenterZ=0 NormalX=0 NormalY=0 NormalZ=1 AngleXU=0 Radius=1.6
    g88: Circle CenterX=-42.7164 CenterY=-63.9296 CenterZ=0 NormalX=0 NormalY=0 NormalZ=1 AngleXU=0 Radius=1.6
    g89: Circle CenterX=-15 CenterY=-75.4101 CenterZ=0 NormalX=0 NormalY=0 NormalZ=1 AngleXU=0 Radius=1.6
    g90: Circle CenterX=15 CenterY=-75.4101 CenterZ=0 NormalX=0 NormalY=0 NormalZ=1 AngleXU=0 Radius=1.6
    g91: Circle CenterX=42.7164 CenterY=-63.9296 CenterZ=0 NormalX=0 NormalY=0 NormalZ=1 AngleXU=0 Radius=1.6
    g92: Circle CenterX=63.9296 CenterY=-42.7164 CenterZ=0 NormalX=0 NormalY=0 NormalZ=1 AngleXU=0 Radius=1.6
    g93: Circle CenterX=75.4101 CenterY=-15 CenterZ=0 NormalX=0 NormalY=0 NormalZ=1 AngleXU=0 Radius=1.6
    g94: Circle CenterX=75.4101 CenterY=15 CenterZ=0 NormalX=0 NormalY=0 NormalZ=1 AngleXU=0 Radius=1.6
    g95: Circle CenterX=63.9296 CenterY=42.7164 CenterZ=0 NormalX=0 NormalY=0 NormalZ=1 AngleXU=0 Radius=1.6
    g96: Circle CenterX=42.7164 CenterY=63.9296 CenterZ=0 NormalX=0 NormalY=0 NormalZ=1 AngleXU=0 Radius=1.6
    g97: Circle CenterX=15 CenterY=75.4101 CenterZ=0 NormalX=0 NormalY=0 NormalZ=1 AngleXU=0 Radius=1.6
    g98: Circle CenterX=-15 CenterY=75.4101 CenterZ=0 NormalX=0 NormalY=0 NormalZ=1 AngleXU=0 Radius=1.6
    g99: Circle CenterX=-42.7164 CenterY=63.9296 CenterZ=0 NormalX=0 NormalY=0 NormalZ=1 AngleXU=0 Radius=1.6
    g100: Circle CenterX=-63.9296 CenterY=42.7164 CenterZ=0 NormalX=0 NormalY=0 NormalZ=1 AngleXU=0 Radius=1.6
    g101: Circle CenterX=-34.1731 CenterY=51.1437 CenterZ=0 NormalX=0 NormalY=0 NormalZ=1 AngleXU=0 Radius=1.6
    g102: Circle CenterX=-12 CenterY=60.3281 CenterZ=0 NormalX=0 NormalY=0 NormalZ=1 AngleXU=0 Radius=1.6
    g103: Circle CenterX=12 CenterY=60.3281 CenterZ=0 NormalX=0 NormalY=0 NormalZ=1 AngleXU=0 Radius=1.6
    g104: Circle CenterX=34.1731 CenterY=51.1437 CenterZ=0 NormalX=0 NormalY=0 NormalZ=1 AngleXU=0 Radius=1.6
    g105: Circle CenterX=51.1437 CenterY=34.1731 CenterZ=0 NormalX=0 NormalY=0 NormalZ=1 AngleXU=0 Radius=1.6
    g106: Circle CenterX=60.3281 CenterY=12 CenterZ=0 NormalX=0 NormalY=0 NormalZ=1 AngleXU=0 Radius=1.6
    g107: Circle CenterX=60.3281 CenterY=-12 CenterZ=0 NormalX=0 NormalY=0 NormalZ=1 AngleXU=0 Radius=1.6
    g108: Circle CenterX=51.1437 CenterY=-34.1731 CenterZ=0 NormalX=0 NormalY=0 NormalZ=1 AngleXU=0 Radius=1.6
    g109: Circle CenterX=34.1731 CenterY=-51.1437 CenterZ=0 NormalX=0 NormalY=0 NormalZ=1 AngleXU=0 Radius=1.6
    g110: Circle CenterX=12 CenterY=-60.3281 CenterZ=0 NormalX=0 NormalY=0 NormalZ=1 AngleXU=0 Radius=1.6
    g111: Circle CenterX=-12 CenterY=-60.3281 CenterZ=0 NormalX=0 NormalY=0 NormalZ=1 AngleXU=0 Radius=1.6
    g112: Circle CenterX=-34.1731 CenterY=-51.1437 CenterZ=0 NormalX=0 NormalY=0 NormalZ=1 AngleXU=0 Radius=1.6
    g113: Circle CenterX=-51.1437 CenterY=-34.1731 CenterZ=0 NormalX=0 NormalY=0 NormalZ=1 AngleXU=0 Radius=1.6
    g114: Circle CenterX=-60.3281 CenterY=-12 CenterZ=0 NormalX=0 NormalY=0 NormalZ=1 AngleXU=0 Radius=1.6
    g115: Circle CenterX=-60.3281 CenterY=12 CenterZ=0 NormalX=0 NormalY=0 NormalZ=1 AngleXU=0 Radius=1.6
    g116: Circle CenterX=-51.1437 CenterY=34.1731 CenterZ=0 NormalX=0 NormalY=0 NormalZ=1 AngleXU=0 Radius=1.6
    g117: Circle CenterX=-25.6298 CenterY=38.3578 CenterZ=0 NormalX=0 NormalY=0 NormalZ=1 AngleXU=0 Radius=1.6
    g118: Circle CenterX=-9 CenterY=45.2461 CenterZ=0 NormalX=0 NormalY=0 NormalZ=1 AngleXU=0 Radius=1.6
    g119: Circle CenterX=9 CenterY=45.2461 CenterZ=0 NormalX=0 NormalY=0 NormalZ=1 AngleXU=0 Radius=1.6
    g120: Circle CenterX=25.6298 CenterY=38.3578 CenterZ=0 NormalX=0 NormalY=0 NormalZ=1 AngleXU=0 Radius=1.6
    g121: Circle CenterX=38.3578 CenterY=25.6298 CenterZ=0 NormalX=0 NormalY=0 NormalZ=1 AngleXU=0 Radius=1.6
    g122: Circle CenterX=45.2461 CenterY=9 CenterZ=0 NormalX=0 NormalY=0 NormalZ=1 AngleXU=0 Radius=1.6
    g123: Circle CenterX=45.2461 CenterY=-9 CenterZ=0 NormalX=0 NormalY=0 NormalZ=1 AngleXU=0 Radius=1.6
    g124: Circle CenterX=38.3578 CenterY=-25.6298 CenterZ=0 NormalX=0 NormalY=0 NormalZ=1 AngleXU=0 Radius=1.6
    g125: Circle CenterX=25.6298 CenterY=-38.3578 CenterZ=0 NormalX=0 NormalY=0 NormalZ=1 AngleXU=0 Radius=1.6
    g126: Circle CenterX=9 CenterY=-45.2461 CenterZ=0 NormalX=0 NormalY=0 NormalZ=1 AngleXU=0 Radius=1.6
    g127: Circle CenterX=-9 CenterY=-45.2461 CenterZ=0 NormalX=0 NormalY=0 NormalZ=1 AngleXU=0 Radius=1.6
    g128: Circle CenterX=-25.6298 CenterY=-38.3578 CenterZ=0 NormalX=0 NormalY=0 NormalZ=1 AngleXU=0 Radius=1.6
    g129: Circle CenterX=-38.3578 CenterY=-25.6298 CenterZ=0 NormalX=0 NormalY=0 NormalZ=1 AngleXU=0 Radius=1.6
    g130: Circle CenterX=-45.2461 CenterY=-9 CenterZ=0 NormalX=0 NormalY=0 NormalZ=1 AngleXU=0 Radius=1.6
    g131: Circle CenterX=-45.2461 CenterY=9 CenterZ=0 NormalX=0 NormalY=0 NormalZ=1 AngleXU=0 Radius=1.6
    g132: Circle CenterX=-38.3578 CenterY=25.6298 CenterZ=0 NormalX=0 NormalY=0 NormalZ=1 AngleXU=0 Radius=1.6
  constraints (228):
    c: Coincident(g0,g1)
    c: Coincident(g1,g2)
    c: Coincident(g2,g3)
    c: Coincident(g3,g4)
    c: Coincident(g4,g5)
    c: Coincident(g5,g6)
    c: Coincident(g6,g7)
    c: Coincident(g7,g8)
    c: Coincident(g8,g9)
    c: Coincident(g9,g10)
    c: Coincident(g10,g11)
    c: Coincident(g11,g12)
    c: Coincident(g12,g13)
    c: Coincident(g13,g14)
    c: Coincident(g14,g15)
    c: Coincident(g15,g0)
    c: Equal(g0, g1-g15) x15
    c: PointOnObject(g0,g16)
    c: PointOnObject(g1,g16)
    c: PointOnObject(g2,g16)
    c: PointOnObject(g3,g16)
    c: PointOnObject(g4,g16)
    c: PointOnObject(g5,g16)
    c: PointOnObject(g6,g16)
    c: PointOnObject(g7,g16)
    c: PointOnObject(g8,g16)
    c: PointOnObject(g9,g16)
    c: PointOnObject(g10,g16)
    c: PointOnObject(g11,g16)
    c: PointOnObject(g12,g16)
    c: PointOnObject(g13,g16)
    c: PointOnObject(g14,g16)
    c: PointOnObject(g15,g16)
    c: Distance(g7) = 36
    c: Radius(g16) = 92.265
    c: Horizontal(g5)
    c: Distance(g16,g2) = 90.4921
    c: Coincident(g17,g18)
    c: Coincident(g18,g19)
    c: Coincident(g19,g20)
    c: Coincident(g20,g21)
    c: Coincident(g21,g22)
    c: Coincident(g22,g23)
    c: Coincident(g23,g24)
    c: Coincident(g24,g25)
    c: Coincident(g25,g26)
    c: Coincident(g26,g27)
    c: Coincident(g27,g28)
    c: Coincident(g28,g29)
    c: Coincident(g29,g30)
    c: Coincident(g30,g31)
    c: Coincident(g31,g32)
    c: Coincident(g32,g17)
    c: Equal(g17, g18-g32) x15
    c: PointOnObject(g17,g33)
    c: PointOnObject(g18,g33)
    c: PointOnObject(g19,g33)
    c: PointOnObject(g20,g33)
    c: PointOnObject(g21,g33)
    c: PointOnObject(g22,g33)
    c: PointOnObject(g23,g33)
    c: PointOnObject(g24,g33)
    c: PointOnObject(g25,g33)
    c: PointOnObject(g26,g33)
    c: PointOnObject(g27,g33)
    c: PointOnObject(g28,g33)
    c: PointOnObject(g29,g33)
    c: PointOnObject(g30,g33)
    c: PointOnObject(g31,g33)
    c: PointOnObject(g32,g33)
    c: Horizontal(g22)
    c: Distance(g33,g19) = 60.3281
    c: Distance(g24) = 24
    c: Radius(g33) = 61.51
    c: Coincident(g34,g35)
    c: Coincident(g35,g36)
    c: Coincident(g36,g37)
    c: Coincident(g37,g38)
    c: Coincident(g38,g39)
    c: Coincident(g39,g40)
    c: Coincident(g40,g41)
    c: Coincident(g41,g42)
    c: Coincident(g42,g43)
    c: Coincident(g43,g44)
    c: Coincident(g44,g45)
    c: Coincident(g45,g46)
    c: Coincident(g46,g47)
    c: Coincident(g47,g48)
    c: Coincident(g48,g49)
    c: Coincident(g49,g34)
    c: Equal(g34, g35-g49) x15
    c: PointOnObject(g34,g50)
    c: PointOnObject(g35,g50)
    c: PointOnObject(g36,g50)
    c: PointOnObject(g37,g50)
    c: PointOnObject(g38,g50)
    c: PointOnObject(g39,g50)
    c: PointOnObject(g40,g50)
    c: PointOnObject(g41,g50)
    c: PointOnObject(g42,g50)
    c: PointOnObject(g43,g50)
    c: PointOnObject(g44,g50)
    c: PointOnObject(g45,g50)
    c: PointOnObject(g46,g50)
    c: PointOnObject(g47,g50)
    c: PointOnObject(g48,g50)
    c: PointOnObject(g49,g50)
    c: Horizontal(g39)
    c: Distance(g50,g36) = 75.4101
    c: Distance(g41) = 30
    c: Radius(g50) = 76.8875
    c: Coincident(g16,g-1)
    c: Coincident(g16,g33)
    c: Coincident(g51,g52)
    c: Coincident(g52,g53)
    c: Coincident(g53,g54)
    c: Coincident(g54,g55)
    c: Coincident(g55,g56)
    c: Coincident(g56,g57)
    c: Coincident(g57,g58)
    c: Coincident(g58,g59)
    c: Coincident(g59,g60)
    c: Coincident(g60,g61)
    c: Coincident(g61,g62)
    c: Coincident(g62,g63)
    c: Coincident(g63,g64)
    c: Coincident(g64,g65)
    c: Coincident(g65,g66)
    c: Coincident(g66,g51)
    c: Equal(g51, g52-g66) x15
    c: PointOnObject(g51,g67)
    c: PointOnObject(g52,g67)
    c: PointOnObject(g53,g67)
    c: PointOnObject(g54,g67)
    c: PointOnObject(g55,g67)
    c: PointOnObject(g56,g67)
    c: PointOnObject(g57,g67)
    c: PointOnObject(g58,g67)
    c: PointOnObject(g59,g67)
    c: PointOnObject(g60,g67)
    c: PointOnObject(g61,g67)
    c: PointOnObject(g62,g67)
    c: PointOnObject(g63,g67)
    c: PointOnObject(g64,g67)
    c: PointOnObject(g65,g67)
    c: PointOnObject(g66,g67)
    c: Horizontal(g56)
    c: Distance(g67,g53) = 45.2461
    c: Coincident(g16,g67)
    c: Radius(g67) = 46.1325
    c: Distance(g58) = 18
    c: Coincident(g16,g50)
    c: Coincident(g68,g5)
    c: Coincident(g69,g4)
    c: Coincident(g70,g3)
    c: Coincident(g71,g2)
    c: Coincident(g72,g1)
    c: Coincident(g73,g0)
    c: Coincident(g74,g0)
    c: Coincident(g75,g14)
    c: Coincident(g76,g13)
    c: Coincident(g77,g12)
    c: Coincident(g78,g11)
    c: Coincident(g79,g10)
    c: Coincident(g80,g9)
    c: Coincident(g81,g8)
    c: Coincident(g82,g7)
    c: Coincident(g83,g6)
    c: Equal(g69,g68)
    c: Equal(g69, g70-g83) x14
    c: Radius(g69) = 1.6
    c: Coincident(g84,g-1)
    c: Coincident(g85,g42)
    c: Coincident(g86,g43)
    c: Coincident(g87,g44)
    c: Coincident(g88,g45)
    c: Coincident(g89,g46)
    c: Coincident(g90,g47)
    c: Coincident(g91,g48)
    c: Coincident(g92,g34)
    c: Coincident(g93,g34)
    c: Coincident(g94,g35)
    c: Coincident(g95,g36)
    c: Coincident(g97,g38)
    c: Coincident(g98,g39)
    c: Coincident(g99,g40)
    c: Coincident(g100,g41)
    c: Equal(g99,g100)
    c: Equal(g99, g85-g98) x14
    c: Radius(g99) = 1.6
    c: Coincident(g37,g96)
    c: Coincident(g101,g23)
    c: Coincident(g102,g22)
    c: Coincident(g103,g21)
    c: Coincident(g104,g20)
    c: Coincident(g105,g19)
    c: Coincident(g106,g18)
    c: Coincident(g107,g17)
    c: Coincident(g109,g31)
    c: Coincident(g110,g30)
    c: Coincident(g111,g29)
    c: Coincident(g112,g28)
    c: Coincident(g113,g27)
    c: Coincident(g114,g26)
    c: Coincident(g115,g25)
    c: Coincident(g116,g24)
    c: Coincident(g17,g108)
    c: Equal(g116, g101-g115) x15
    c: Radius(g116) = 1.6
    c: Coincident(g117,g57)
    c: Coincident(g118,g56)
    c: Coincident(g119,g55)
    c: Coincident(g120,g54)
    c: Coincident(g121,g53)
    c: Coincident(g122,g52)
    c: Coincident(g123,g51)
    c: Coincident(g124,g51)
    c: Coincident(g125,g65)
    c: Coincident(g126,g64)
    c: Coincident(g127,g63)
    c: Coincident(g128,g62)
    c: Coincident(g129,g61)
    c: Coincident(g130,g60)
    c: Coincident(g131,g59)
    c: Coincident(g132,g58)
    c: Equal(g117, g118-g132) x15
    c: Radius(g117) = 1.6
    c: Radius(g84) = 100
FEATURE [PartDesign::Pad] Pad029
  Direction = (1,1,1)
  Length = 10
  Length2 = 100
  Profile = -> Sketch085
  Type = 0
FEATURE [Sketcher::SketchObject] Sketch086
  FullyConstrained = true
  MapMode = 5
  Placement = pos=(0,0,0) rot=(1,0,0;3.14159rad)
  Support = -> [Pad029]
  sketch-geometry (1):
    g0: Circle CenterX=0 CenterY=0 CenterZ=0 NormalX=0 NormalY=0 NormalZ=1 AngleXU=0 Radius=32.5
  constraints (2):
    c: Coincident(g0,g-1)
    c: Radius(g0) = 32.5
FEATURE [PartDesign::Pocket] Pocket051
  BaseFeature = -> Pad029
  Length = 8
  Length2 = 100
  Profile = -> Sketch086
  Type = 0
FEATURE [Sketcher::SketchObject] Sketch087
  FullyConstrained = true
  MapMode = 5
  Placement = pos=(0,0,10) rot=(0,0,1;0rad)
  Support = -> [Pocket051]
  sketch-geometry (1):
    g0: Circle CenterX=0 CenterY=0 CenterZ=0 NormalX=0 NormalY=0 NormalZ=1 AngleXU=0 Radius=4.5
  constraints (2):
    c: Coincident(g0,g-1)
    c: Radius(g0) = 4.5
FEATURE [PartDesign::Pocket] Pocket052
  BaseFeature = -> Pocket051
  Length = 5
  Length2 = 100
  Profile = -> Sketch087
  Type = 0
FEATURE [PartDesign::Chamfer] Chamfer009
  Angle = 45
  Base = -> Pocket052 [Edge52]
  BaseFeature = -> Pocket052
  ChamferType = 0
  FlipDirection = false
  Size = 1
  Size2 = 1
  SupportTransform = false
FEATURE [PartDesign::Body] Body019  label="CARCASA"
  Group = -> [Sketch085,Pad029,Sketch086,Pocket051,Sketch087,Pocket052,Chamfer009]
  Origin = -> Origin019
  Tip = -> Chamfer009
COMPONENT P11 — recipe-attached ("POLEA", modeled in this document).
Construction recipe (the document's own serialized feature program — sketch geometry with constraints, then the solid features built on it; lengths are millimeters unless a unit is written):

FEATURE [Sketcher::SketchObject] Sketch091
  FullyConstrained = true
  MapMode = 5
  Placement = pos=(0,0,0) rot=(0.57735,0.57735,0.57735;2.0944rad)
  Support = -> [YZ_Plane021]
  sketch-geometry (8):
    g0: LineSegment StartX=1.55 StartY=4.1 StartZ=0 EndX=1.55 EndY=-4.1 EndZ=0
    g1: LineSegment StartX=1.55 StartY=-4.1 StartZ=0 EndX=9 EndY=-4.1 EndZ=0
    g2: LineSegment StartX=9 StartY=-4.1 StartZ=0 EndX=9 EndY=-3.1 EndZ=0
    g3: LineSegment StartX=9 StartY=-3.1 StartZ=0 EndX=6 EndY=-3.1 EndZ=0
    g4: LineSegment StartX=6 StartY=-3.1 StartZ=0 EndX=6 EndY=3.1 EndZ=0
    g5: LineSegment StartX=6 StartY=3.1 StartZ=0 EndX=9 EndY=3.1 EndZ=0
    g6: LineSegment StartX=9 StartY=3.1 StartZ=0 EndX=9 EndY=4.1 EndZ=0
    g7: LineSegment StartX=9 StartY=4.1 StartZ=0 EndX=1.55 EndY=4.1 EndZ=0
  constraints (22):
    c: Coincident(g0,g1)
    c: Horizontal(g1)
    c: Coincident(g1,g2)
    c: Vertical(g2)
    c: Coincident(g2,g3)
    c: Horizontal(g3)
    c: Coincident(g3,g4)
    c: Coincident(g4,g5)
    c: Horizontal(g5)
    c: Coincident(g5,g6)
    c: Vertical(g6)
    c: Coincident(g6,g7)
    c: Coincident(g7,g0)
    c: Horizontal(g7)
    c: Vertical(g5,g2)
    c: DistanceX(g-1,g0) = 1.55
    c: DistanceX(g-1,g4) = 6
    c: DistanceY(g0,g0) = 8.2
    c: Symmetric(g0,g0,g-1)
    c: DistanceY(g3,g4) = 6.2
    c: Symmetric(g4,g3,g-1)
    c: DistanceX(g-1,g6) = 9
FEATURE [PartDesign::Revolution] Revolution001
  Angle = 360
  Axis = (-2e-16,3e-16,1)
  Base = (0,0,0)
  Placement = pos=(0,0,0) rot=(0.57735,0.57735,0.57735;2.0944rad)
  Profile = -> Sketch091
  ReferenceAxis = -> Sketch091 [V_Axis]
  Reversed = true
FEATURE [PartDesign::Body] Body021  label="POLEA"
  Group = -> [Sketch091,Revolution001]
  Origin = -> Origin021
  Tip = -> Revolution001
COMPONENT P12 — recipe-attached ("ALEROS", modeled in this document).
Construction recipe (the document's own serialized feature program — sketch geometry with constraints, then the solid features built on it; lengths are millimeters unless a unit is written):

FEATURE [Sketcher::SketchObject] Sketch100
  FullyConstrained = true
  Placement = pos=(0,0,120) rot=(0,1,0;1.5708rad)
  sketch-geometry (6):
    g0: LineSegment StartX=7 StartY=252.37 StartZ=0 EndX=113 EndY=252.37 EndZ=0
    g1: LineSegment StartX=113 StartY=252.37 StartZ=0 EndX=113 EndY=9 EndZ=0
    g2: LineSegment StartX=111 StartY=7 StartZ=0 EndX=9 EndY=7 EndZ=0
    g3: LineSegment StartX=7 StartY=9 StartZ=0 EndX=7 EndY=252.37 EndZ=0
    g4: LineSegment StartX=7 StartY=9 StartZ=0 EndX=9 EndY=7 EndZ=0
    g5: LineSegment StartX=113 StartY=9 StartZ=0 EndX=111 EndY=7 EndZ=0
  constraints (18):
    c: Horizontal(g0)
    c: Horizontal(g2)
    c: Vertical(g1)
    c: Vertical(g3)
    c: Coincident(g4,g3)
    c: Coincident(g4,g2)
    c: Coincident(g5,g1)
    c: Coincident(g5,g2)
    c: DistanceY(g-1,g2) = 7
    c: DistanceX(g-1,g3) = 7
    c: DistanceX(g3,g1) = 106
    c: Horizontal(g1,g3)
    c: DistanceX(g3,g2) = 2
    c: DistanceX(g2,g1) = 2
    c: DistanceY(g2,g3) = 2
    c: Coincident(g0,g3)
    c: Coincident(g0,g1)
    c: DistanceY(g0) = 252.37
FEATURE [Sketcher::SketchObject] Sketch102
  FullyConstrained = true
  MapMode = 3
  Placement = pos=(-2.8e-15,0,0) rot=(0,0,1;0rad)
  sketch-geometry (15):
    g0: LineSegment StartX=-50 StartY=0 StartZ=0 EndX=50 EndY=0 EndZ=0
    g1: LineSegment StartX=-50 StartY=0 StartZ=0 EndX=-30 EndY=215 EndZ=0
    g2: LineSegment StartX=50 StartY=0 StartZ=0 EndX=30 EndY=215 EndZ=0
    g3: Circle CenterX=0 CenterY=221.15 CenterZ=0 NormalX=0 NormalY=0 NormalZ=1 AngleXU=0 Radius=9.5
    g4: ArcOfCircle CenterX=0 CenterY=211.65 CenterZ=0 NormalX=0 NormalY=0 NormalZ=1 AngleXU=0 Radius=30.1865 StartAngle=0.111206 EndAngle=3.03039
    g5: Circle CenterX=0 CenterY=21.15 CenterZ=0 NormalX=0 NormalY=0 NormalZ=1 AngleXU=0 Radius=11
    g6: Circle CenterX=0 CenterY=101.15 CenterZ=0 NormalX=0 NormalY=0 NormalZ=1 AngleXU=0 Radius=9.5
    g7: Circle CenterX=-15.5 CenterY=36.65 CenterZ=0 NormalX=0 NormalY=0 NormalZ=1 AngleXU=0 Radius=1.65
    g8: Circle CenterX=15.5 CenterY=36.65 CenterZ=0 NormalX=0 NormalY=0 NormalZ=1 AngleXU=0 Radius=1.65
    g9: Circle CenterX=-30.5907 CenterY=101.15 CenterZ=0 NormalX=0 NormalY=0 NormalZ=1 AngleXU=0 Radius=1.6
    g10: Circle CenterX=30.5907 CenterY=101.15 CenterZ=0 NormalX=0 NormalY=0 NormalZ=1 AngleXU=0 Radius=1.6
    g11: Circle CenterX=-25.0093 CenterY=161.15 CenterZ=0 NormalX=0 NormalY=0 NormalZ=1 AngleXU=0 Radius=1.6
    g12: Circle CenterX=25.0093 CenterY=161.15 CenterZ=0 NormalX=0 NormalY=0 NormalZ=1 AngleXU=0 Radius=1.6
    g13: GeomPoint X=-40.5907 Y=101.15 Z=0
    g14: GeomPoint X=-35.0093 Y=161.15 Z=0
  constraints (41):
    c: PointOnObject(g0,g-1)
    c: Coincident(g1,g0)
    c: Coincident(g2,g0)
    c: Symmetric(g0,g0,g-1)
    c: DistanceX(g0,g0) = 100
    c: DistanceX(g1,g2) = 60
    c: Symmetric(g1,g2,g-2)
    c: PointOnObject(g4,g-2)
    c: Coincident(g4,g1)
    c: PointOnObject(g4,g2)
    c: Radius(g3) = 9.5
    c: DistanceY(g1) = 215
    c: PointOnObject(g4,g3)
    c: Radius(g5) = 11
    c: DistanceY(g0,g5) = 21.15
    c: PointOnObject(g5,g-2)
    c: Radius(g6) = 9.5
    c: DistanceY(g5,g6) = 80
    c: DistanceY(g6,g3) = 120
    c: PointOnObject(g3,g-2)
    c: PointOnObject(g6,g-2)
    c: Horizontal(g7,g8)
    c: DistanceX(g7,g8) = 31
    c: DistanceY(g5,g7) = 15.5
    c: DistanceX(g7,g5) = 15.5
    c: Equal(g7,g8)
    c: Radius(g7) = 1.65
    c: Equal(g9,g11)
    c: Equal(g9,g12)
    c: Equal(g9,g10)
    c: Radius(g9) = 1.6
    c: Symmetric(g9,g10,g-2)
    c: Symmetric(g11,g12,g-2)
    c: Horizontal(g9,g6)
    c: PointOnObject(g13,g1)
    c: Horizontal(g13,g9)
    c: DistanceX(g13,g9) = 10
    c: PointOnObject(g14,g1)
    c: Horizontal(g11,g14)
    c: DistanceX(g14,g11) = 10
    c: DistanceY(g12,g3) = 60
FEATURE [PartDesign::Pad] Pad032
  Direction = (1,1,1)
  Length = 120
  Length2 = 100
  Placement = pos=(-2.8e-15,0,0) rot=(0,0,1;0rad)
  Profile = -> Sketch102
  Type = 0
FEATURE [PartDesign::Pocket] Pocket061
  BaseFeature = -> Pad032
  Length = 304.8
  Length2 = 100
  Midplane = true
  Placement = pos=(-2.8e-15,0,0) rot=(0,0,1;0rad)
  Profile = -> Sketch100
  Type = 0
FEATURE [Sketcher::SketchObject] Sketch099
  ExternalGeometry = -> [Pocket061]
  FullyConstrained = true
  MapMode = 5
  Placement = pos=(-2.8e-15,0,0) rot=(1,0,0;1.5708rad)
  Support = -> [Pocket061]
  sketch-geometry (5):
    g0: Circle CenterX=-40 CenterY=100 CenterZ=0 NormalX=0 NormalY=0 NormalZ=1 AngleXU=0 Radius=3.1
    g1: Circle CenterX=40 CenterY=100 CenterZ=0 NormalX=0 NormalY=0 NormalZ=1 AngleXU=0 Radius=3.1
    g2: Circle CenterX=-40 CenterY=20 CenterZ=0 NormalX=0 NormalY=0 NormalZ=1 AngleXU=0 Radius=3.1
    g3: Circle CenterX=40 CenterY=20 CenterZ=0 NormalX=0 NormalY=0 NormalZ=1 AngleXU=0 Radius=3.1
    g4: Circle CenterX=-1.7e-14 CenterY=60 CenterZ=0 NormalX=0 NormalY=0 NormalZ=1 AngleXU=0 Radius=14
  constraints (12):
    c: Radius(g4) = 14
    c: Symmetric(g-3,g-4,g4)
    c: Equal(g0,g1)
    c: Equal(g0,g2)
    c: Equal(g0,g3)
    c: Radius(g0) = 3.1
    c: Symmetric(g0,g3,g4)
    c: Symmetric(g2,g1,g4)
    c: DistanceX(g0,g1) = 80
    c: DistanceY(g2,g0) = 80
    c: Horizontal(g1,g0)
    c: Vertical(g0,g2)
FEATURE [PartDesign::Pocket] Pocket059
  BaseFeature = -> Pocket061
  Length = 8
  Length2 = 100
  Placement = pos=(-2.8e-15,0,0) rot=(0,0,1;0rad)
  Profile = -> Sketch099
  Type = 0
FEATURE [Sketcher::SketchObject] Sketch098
  ExternalGeometry = -> [Pocket059]
  FullyConstrained = true
  MapMode = 5
  Placement = pos=(-2.8e-15,0,120) rot=(0,0,1;0rad)
  Support = -> [Pocket059]
  sketch-geometry (2):
    g0: Circle CenterX=0 CenterY=101.15 CenterZ=0 NormalX=0 NormalY=0 NormalZ=1 AngleXU=0 Radius=11.15
    g1: Circle CenterX=0 CenterY=221.15 CenterZ=0 NormalX=0 NormalY=0 NormalZ=1 AngleXU=0 Radius=11.15
  constraints (4):
    c: Radius(g1) = 11.15
    c: Radius(g0) = 11.15
    c: Coincident(g1,g-4)
    c: Coincident(g0,g-3)
FEATURE [PartDesign::Pocket] Pocket060
  BaseFeature = -> Pocket059
  Length = 5
  Length2 = 100
  Placement = pos=(-2.8e-15,0,0) rot=(0,0,1;0rad)
  Profile = -> Sketch098
  Type = 0
FEATURE [Sketcher::SketchObject] Sketch101
  ExternalGeometry = -> [Pocket060]
  FullyConstrained = true
  MapMode = 5
  Placement = pos=(-2.8e-15,0,0) rot=(1,0,0;3.14159rad)
  Support = -> [Pocket060]
  sketch-geometry (2):
    g0: Circle CenterX=0 CenterY=-221.15 CenterZ=0 NormalX=0 NormalY=0 NormalZ=1 AngleXU=0 Radius=11.15
    g1: Circle CenterX=0 CenterY=-101.15 CenterZ=0 NormalX=0 NormalY=0 NormalZ=1 AngleXU=0 Radius=11.15
  constraints (4):
    c: Radius(g1) = 11.15
    c: Radius(g0) = 11.15
    c: Coincident(g0,g-6)
    c: Coincident(g1,g-5)
FEATURE [PartDesign::Pocket] Pocket062
  BaseFeature = -> Pocket060
  Length = 5
  Length2 = 100
  Placement = pos=(-2.8e-15,0,0) rot=(0,0,1;0rad)
  Profile = -> Sketch101
  Type = 0
FEATURE [PartDesign::Chamfer] Chamfer012
  Angle = 45
  Base = -> Pocket062 [Edge28,Edge26,Edge39,Edge37]
  BaseFeature = -> Pocket062
  ChamferType = 0
  FlipDirection = false
  Placement = pos=(-2.8e-15,0,0) rot=(0,0,1;0rad)
  Size = 0.8
  Size2 = 1
  SupportTransform = false
FEATURE [PartDesign::Body] Body024  label="ALEROS"
  Group = -> [Sketch102,Pad032,Sketch100,Pocket061,Sketch099,Pocket059,Sketch098,Pocket060,Sketch101,Pocket062,Chamfer012]
  Origin = -> Origin024
  Placement = pos=(0,60,75.6) rot=(1,0,0;1.5708rad)
  Tip = -> Chamfer012
COMPONENT P13 — recipe-attached ("p_ALEROS001", modeled in this document).
Construction recipe (the document's own serialized feature program — sketch geometry with constraints, then the solid features built on it; lengths are millimeters unless a unit is written):

FEATURE [Sketcher::SketchObject] Sketch105
  FullyConstrained = true
  Placement = pos=(0,0,120) rot=(0,1,0;1.5708rad)
  sketch-geometry (6):
    g0: LineSegment StartX=7 StartY=252.37 StartZ=0 EndX=113 EndY=252.37 EndZ=0
    g1: LineSegment StartX=113 StartY=252.37 StartZ=0 EndX=113 EndY=9 EndZ=0
    g2: LineSegment StartX=111 StartY=7 StartZ=0 EndX=9 EndY=7 EndZ=0
    g3: LineSegment StartX=7 StartY=9 StartZ=0 EndX=7 EndY=252.37 EndZ=0
    g4: LineSegment StartX=7 StartY=9 StartZ=0 EndX=9 EndY=7 EndZ=0
    g5: LineSegment StartX=113 StartY=9 StartZ=0 EndX=111 EndY=7 EndZ=0
  constraints (18):
    c: Horizontal(g0)
    c: Horizontal(g2)
    c: Vertical(g1)
    c: Vertical(g3)
    c: Coincident(g4,g3)
    c: Coincident(g4,g2)
    c: Coincident(g5,g1)
    c: Coincident(g5,g2)
    c: DistanceY(g-1,g2) = 7
    c: DistanceX(g-1,g3) = 7
    c: DistanceX(g3,g1) = 106
    c: Horizontal(g1,g3)
    c: DistanceX(g3,g2) = 2
    c: DistanceX(g2,g1) = 2
    c: DistanceY(g2,g3) = 2
    c: Coincident(g0,g3)
    c: Coincident(g0,g1)
    c: DistanceY(g0) = 252.37
FEATURE [Sketcher::SketchObject] Sketch107
  FullyConstrained = true
  MapMode = 3
  Placement = pos=(-2.8e-15,0,0) rot=(0,0,1;0rad)
  sketch-geometry (15):
    g0: LineSegment StartX=-50 StartY=0 StartZ=0 EndX=50 EndY=0 EndZ=0
    g1: LineSegment StartX=-50 StartY=0 StartZ=0 EndX=-30 EndY=215 EndZ=0
    g2: LineSegment StartX=50 StartY=0 StartZ=0 EndX=30 EndY=215 EndZ=0
    g3: Circle CenterX=0 CenterY=221.15 CenterZ=0 NormalX=0 NormalY=0 NormalZ=1 AngleXU=0 Radius=9.5
    g4: ArcOfCircle CenterX=0 CenterY=211.65 CenterZ=0 NormalX=0 NormalY=0 NormalZ=1 AngleXU=0 Radius=30.1865 StartAngle=0.111206 EndAngle=3.03039
    g5: Circle CenterX=0 CenterY=21.15 CenterZ=0 NormalX=0 NormalY=0 NormalZ=1 AngleXU=0 Radius=11
    g6: Circle CenterX=0 CenterY=101.15 CenterZ=0 NormalX=0 NormalY=0 NormalZ=1 AngleXU=0 Radius=9.5
    g7: Circle CenterX=-15.5 CenterY=36.65 CenterZ=0 NormalX=0 NormalY=0 NormalZ=1 AngleXU=0 Radius=1.65
    g8: Circle CenterX=15.5 CenterY=36.65 CenterZ=0 NormalX=0 NormalY=0 NormalZ=1 AngleXU=0 Radius=1.65
    g9: Circle CenterX=-30.5907 CenterY=101.15 CenterZ=0 NormalX=0 NormalY=0 NormalZ=1 AngleXU=0 Radius=1.6
    g10: Circle CenterX=30.5907 CenterY=101.15 CenterZ=0 NormalX=0 NormalY=0 NormalZ=1 AngleXU=0 Radius=1.6
    g11: Circle CenterX=-25.0093 CenterY=161.15 CenterZ=0 NormalX=0 NormalY=0 NormalZ=1 AngleXU=0 Radius=1.6
    g12: Circle CenterX=25.0093 CenterY=161.15 CenterZ=0 NormalX=0 NormalY=0 NormalZ=1 AngleXU=0 Radius=1.6
    g13: GeomPoint X=-40.5907 Y=101.15 Z=0
    g14: GeomPoint X=-35.0093 Y=161.15 Z=0
  constraints (41):
    c: PointOnObject(g0,g-1)
    c: Coincident(g1,g0)
    c: Coincident(g2,g0)
    c: Symmetric(g0,g0,g-1)
    c: DistanceX(g0,g0) = 100
    c: DistanceX(g1,g2) = 60
    c: Symmetric(g1,g2,g-2)
    c: PointOnObject(g4,g-2)
    c: Coincident(g4,g1)
    c: PointOnObject(g4,g2)
    c: Radius(g3) = 9.5
    c: DistanceY(g1) = 215
    c: PointOnObject(g4,g3)
    c: Radius(g5) = 11
    c: DistanceY(g0,g5) = 21.15
    c: PointOnObject(g5,g-2)
    c: Radius(g6) = 9.5
    c: DistanceY(g5,g6) = 80
    c: DistanceY(g6,g3) = 120
    c: PointOnObject(g3,g-2)
    c: PointOnObject(g6,g-2)
    c: Horizontal(g7,g8)
    c: DistanceX(g7,g8) = 31
    c: DistanceY(g5,g7) = 15.5
    c: DistanceX(g7,g5) = 15.5
    c: Equal(g7,g8)
    c: Radius(g7) = 1.65
    c: Equal(g9,g11)
    c: Equal(g9,g12)
    c: Equal(g9,g10)
    c: Radius(g9) = 1.6
    c: Symmetric(g9,g10,g-2)
    c: Symmetric(g11,g12,g-2)
    c: Horizontal(g9,g6)
    c: PointOnObject(g13,g1)
    c: Horizontal(g13,g9)
    c: DistanceX(g13,g9) = 10
    c: PointOnObject(g14,g1)
    c: Horizontal(g11,g14)
    c: DistanceX(g14,g11) = 10
    c: DistanceY(g12,g3) = 60
FEATURE [PartDesign::Pad] Pad033
  Direction = (1,1,1)
  Length = 120
  Length2 = 100
  Placement = pos=(-2.8e-15,0,0) rot=(0,0,1;0rad)
  Profile = -> Sketch107
  Type = 0
FEATURE [PartDesign::Pocket] Pocket065
  BaseFeature = -> Pad033
  Length = 304.8
  Length2 = 100
  Midplane = true
  Placement = pos=(-2.8e-15,0,0) rot=(0,0,1;0rad)
  Profile = -> Sketch105
  Type = 0
FEATURE [Sketcher::SketchObject] Sketch104
  ExternalGeometry = -> [Pocket065]
  FullyConstrained = true
  MapMode = 5
  Placement = pos=(-2.8e-15,0,0) rot=(1,0,0;1.5708rad)
  Support = -> [Pocket065]
  sketch-geometry (5):
    g0: Circle CenterX=-40 CenterY=100 CenterZ=0 NormalX=0 NormalY=0 NormalZ=1 AngleXU=0 Radius=3.1
    g1: Circle CenterX=40 CenterY=100 CenterZ=0 NormalX=0 NormalY=0 NormalZ=1 AngleXU=0 Radius=3.1
    g2: Circle CenterX=-40 CenterY=20 CenterZ=0 NormalX=0 NormalY=0 NormalZ=1 AngleXU=0 Radius=3.1
    g3: Circle CenterX=40 CenterY=20 CenterZ=0 NormalX=0 NormalY=0 NormalZ=1 AngleXU=0 Radius=3.1
    g4: Circle CenterX=-1.7e-14 CenterY=60 CenterZ=0 NormalX=0 NormalY=0 NormalZ=1 AngleXU=0 Radius=14
  constraints (12):
    c: Radius(g4) = 14
    c: Symmetric(g-3,g-4,g4)
    c: Equal(g0,g1)
    c: Equal(g0,g2)
    c: Equal(g0,g3)
    c: Radius(g0) = 3.1
    c: Symmetric(g0,g3,g4)
    c: Symmetric(g2,g1,g4)
    c: DistanceX(g0,g1) = 80
    c: DistanceY(g2,g0) = 80
    c: Horizontal(g1,g0)
    c: Vertical(g0,g2)
FEATURE [PartDesign::Pocket] Pocket063
  BaseFeature = -> Pocket065
  Length = 8
  Length2 = 100
  Placement = pos=(-2.8e-15,0,0) rot=(0,0,1;0rad)
  Profile = -> Sketch104
  Type = 0
FEATURE [Sketcher::SketchObject] Sketch103
  ExternalGeometry = -> [Pocket063]
  FullyConstrained = true
  MapMode = 5
  Placement = pos=(-2.8e-15,0,120) rot=(0,0,1;0rad)
  Support = -> [Pocket063]
  sketch-geometry (2):
    g0: Circle CenterX=0 CenterY=101.15 CenterZ=0 NormalX=0 NormalY=0 NormalZ=1 AngleXU=0 Radius=11.15
    g1: Circle CenterX=0 CenterY=221.15 CenterZ=0 NormalX=0 NormalY=0 NormalZ=1 AngleXU=0 Radius=11.15
  constraints (4):
    c: Radius(g1) = 11.15
    c: Radius(g0) = 11.15
    c: Coincident(g1,g-4)
    c: Coincident(g0,g-3)
FEATURE [PartDesign::Pocket] Pocket064
  BaseFeature = -> Pocket063
  Length = 5
  Length2 = 100
  Placement = pos=(-2.8e-15,0,0) rot=(0,0,1;0rad)
  Profile = -> Sketch103
  Type = 0
FEATURE [Sketcher::SketchObject] Sketch106
  ExternalGeometry = -> [Pocket064]
  FullyConstrained = true
  MapMode = 5
  Placement = pos=(-2.8e-15,0,0) rot=(1,0,0;3.14159rad)
  Support = -> [Pocket064]
  sketch-geometry (2):
    g0: Circle CenterX=0 CenterY=-221.15 CenterZ=0 NormalX=0 NormalY=0 NormalZ=1 AngleXU=0 Radius=11.15
    g1: Circle CenterX=0 CenterY=-101.15 CenterZ=0 NormalX=0 NormalY=0 NormalZ=1 AngleXU=0 Radius=11.15
  constraints (4):
    c: Radius(g1) = 11.15
    c: Radius(g0) = 11.15
    c: Coincident(g0,g-6)
    c: Coincident(g1,g-5)
FEATURE [PartDesign::Pocket] Pocket066
  BaseFeature = -> Pocket064
  Length = 5
  Length2 = 100
  Placement = pos=(-2.8e-15,0,0) rot=(0,0,1;0rad)
  Profile = -> Sketch106
  Type = 0
FEATURE [PartDesign::Chamfer] Chamfer013
  Angle = 45
  Base = -> Pocket066 [Edge28,Edge26,Edge39,Edge37]
  BaseFeature = -> Pocket066
  ChamferType = 0
  FlipDirection = false
  Placement = pos=(-2.8e-15,0,0) rot=(0,0,1;0rad)
  Size = 0.8
  Size2 = 1
  SupportTransform = false
FEATURE [PartDesign::Body] Body025  label="p_ALEROS001"
  Group = -> [Sketch107,Pad033,Sketch105,Pocket065,Sketch104,Pocket063,Sketch103,Pocket064,Sketch106,Pocket066,Chamfer013]
  Origin = -> Origin025
  Placement = pos=(1,0,0) rot=(1,0,0;1.5708rad)
  Tip = -> Chamfer013
COMPONENT P14 — recipe-attached ("SOP_POLEA", modeled in this document).
Construction recipe (the document's own serialized feature program — sketch geometry with constraints, then the solid features built on it; lengths are millimeters unless a unit is written):

FEATURE [Sketcher::SketchObject] Sketch108
  FullyConstrained = true
  MapMode = 5
  Placement = pos=(0,0,0) rot=(1,0,0;1.5708rad)
  Support = -> [XZ_Plane026]
  sketch-geometry (6):
    g0: LineSegment StartX=40.3584 StartY=55.5 StartZ=0 EndX=40.3584 EndY=47.5 EndZ=0
    g1: LineSegment StartX=40.3584 StartY=47.5 StartZ=0 EndX=38 EndY=0 EndZ=0
    g2: LineSegment StartX=38 StartY=0 StartZ=0 EndX=0 EndY=0 EndZ=0
    g3: LineSegment StartX=0 StartY=0 StartZ=0 EndX=0 EndY=15 EndZ=0
    g4: LineSegment StartX=0 StartY=15 StartZ=0 EndX=28.3584 EndY=55.5 EndZ=0
    g5: LineSegment StartX=28.3584 StartY=55.5 StartZ=0 EndX=40.3584 EndY=55.5 EndZ=0
  constraints (17):
    c: Coincident(g1,g2)
    c: Horizontal(g2)
    c: Coincident(g2,g3)
    c: Vertical(g3)
    c: Coincident(g4,g5)
    c: Coincident(g5,g0)
    c: DistanceX(g2,g2) = 38
    c: Coincident(g3,g4)
    c: Horizontal(g5)
    c: DistanceY(g1,g4) = 55.5
    c: Vertical(g0)
    c: Coincident(g0,g1)
    c: DistanceX(g5,g5) = 12
    c: DistanceY(g3,g3) = 15
    c: DistanceY(g0,g0) = 8
    c: Coincident(g2,g-1)
    c: Angle(g4,g5) = 2.18166
FEATURE [PartDesign::Pad] Pad034
  Direction = (1,1,1)
  Length = 13.2
  Length2 = 100
  Placement = pos=(0,0,0) rot=(1,0,0;1.5708rad)
  Profile = -> Sketch108
  Type = 0
FEATURE [Sketcher::SketchObject] Sketch109
  ExternalGeometry = -> [Pad034]
  FullyConstrained = true
  MapMode = 5
  Placement = pos=(0,0,0) rot=(1,0,0;3.14159rad)
  Support = -> [Pad034]
  sketch-geometry (2):
    g0: Circle CenterX=4.98091 CenterY=6.6 CenterZ=0 NormalX=0 NormalY=0 NormalZ=1 AngleXU=0 Radius=1.55
    g1: Circle CenterX=20.3584 CenterY=6.6 CenterZ=0 NormalX=0 NormalY=0 NormalZ=1 AngleXU=0 Radius=1.55
  constraints (7):
    c: Equal(g0,g1)
    c: Radius(g0) = 1.55
    c: Horizontal(g0,g1)
    c: DistanceY(g-3,g-3) = 13.2
    c: DistanceX(g0,g1) = 15.3775
    c: DistanceY(g-1,g0) = 6.6
    c: DistanceX(g1,g-4) = 20
FEATURE [PartDesign::Pocket] Pocket067
  BaseFeature = -> Pad034
  Length = 80
  Length2 = 100
  Placement = pos=(0,0,0) rot=(1,0,0;1.5708rad)
  Profile = -> Sketch109
  Type = 0
FEATURE [Sketcher::SketchObject] Sketch110
  ExternalGeometry = -> [Pocket067]
  FullyConstrained = true
  MapMode = 5
  Placement = pos=(0,3.67e-14,55.5) rot=(0,0,1;3.14159rad)
  Support = -> [Pocket067]
  sketch-geometry (5):
    g0: LineSegment StartX=-28.3584 StartY=10.3 StartZ=0 EndX=0 EndY=10.3 EndZ=0
    g1: LineSegment StartX=0 StartY=10.3 StartZ=0 EndX=0 EndY=2.9 EndZ=0
    g2: LineSegment StartX=0 StartY=2.9 StartZ=0 EndX=-28.3584 EndY=2.9 EndZ=0
    g3: LineSegment StartX=-28.3584 StartY=2.9 StartZ=0 EndX=-28.3584 EndY=10.3 EndZ=0
    g4: GeomPoint X=-28.3584 Y=6.6 Z=0
  constraints (12):
    c: Coincident(g0,g1)
    c: Coincident(g1,g2)
    c: Coincident(g2,g3)
    c: Coincident(g3,g0)
    c: Horizontal(g0)
    c: Horizontal(g2)
    c: Vertical(g1)
    c: Vertical(g3)
    c: Symmetric(g0,g2,g4)
    c: DistanceY(g3,g3) = 7.4
    c: Vertical(g1,g-1)
    c: Symmetric(g-5,g-5,g4)
FEATURE [PartDesign::Pocket] Pocket068
  BaseFeature = -> Pocket067
  Length = 51
  Length2 = 100
  Placement = pos=(0,0,0) rot=(1,0,0;1.5708rad)
  Profile = -> Sketch110
  Type = 0
FEATURE [Sketcher::SketchObject] Sketch112
  ExternalGeometry = -> [Pocket068]
  FullyConstrained = true
  MapMode = 5
  Placement = pos=(0,3.67e-14,55.5) rot=(0,0,1;3.14159rad)
  Support = -> [Pocket068]
  sketch-geometry (1):
    g0: Circle CenterX=-32.4934 CenterY=6.6 CenterZ=0 NormalX=0 NormalY=0 NormalZ=1 AngleXU=0 Radius=1.55
  constraints (3):
    c: Radius(g0) = 1.55
    c: Horizontal(g0,g-3)
    c: DistanceX(g0,g-3) = 12.135
FEATURE [PartDesign::Pocket] Pocket069
  BaseFeature = -> Pocket068
  Length = 10
  Length2 = 100
  Placement = pos=(0,0,0) rot=(1,0,0;1.5708rad)
  Profile = -> Sketch112
  Type = 0
FEATURE [PartDesign::Fillet] Fillet
  Base = -> Pocket069 [Edge1]
  BaseFeature = -> Pocket069
  Placement = pos=(0,0,0) rot=(1,0,0;1.5708rad)
  Radius = 2
  SupportTransform = false
FEATURE [Sketcher::SketchObject] Sketch113
  ExternalGeometry = -> [Fillet]
  FullyConstrained = true
  MapMode = 5
  Placement = pos=(40.3584,0,0) rot=(0.707107,0,0.707107;3.14159rad)
  Support = -> [Fillet]
  sketch-geometry (5):
    g0: LineSegment StartX=47.5 StartY=10.3 StartZ=0 EndX=50.7 EndY=10.3 EndZ=0
    g1: LineSegment StartX=50.7 StartY=10.3 StartZ=0 EndX=50.7 EndY=2.9 EndZ=0
    g2: LineSegment StartX=50.7 StartY=2.9 StartZ=0 EndX=47.5 EndY=2.9 EndZ=0
    g3: LineSegment StartX=47.5 StartY=2.9 StartZ=0 EndX=47.5 EndY=10.3 EndZ=0
    g4: GeomPoint X=47.5 Y=6.6 Z=0
  constraints (12):
    c: Coincident(g0,g1)
    c: Coincident(g1,g2)
    c: Coincident(g2,g3)
    c: Coincident(g3,g0)
    c: Horizontal(g0)
    c: Horizontal(g2)
    c: Vertical(g1)
    c: Vertical(g3)
    c: DistanceX(g0,g0) = 3.2
    c: DistanceY(g1,g1) = 7.4
    c: Symmetric(g0,g2,g4)
    c: Symmetric(g-3,g-3,g4)
FEATURE [PartDesign::Pocket] Pocket070
  BaseFeature = -> Fillet
  Length = 12
  Length2 = 100
  Placement = pos=(0,0,0) rot=(1,0,0;1.5708rad)
  Profile = -> Sketch113
  Type = 0
FEATURE [PartDesign::Body] Body026  label="SOP_POLEA"
  Group = -> [Sketch108,Pad034,Sketch109,Pocket067,Sketch110,Pocket068,Sketch112,Pocket069,Fillet,Sketch113,Pocket070]
  Origin = -> Origin026
  Tip = -> Pocket070
COMPONENT P15 — recipe-attached ("GRIP TELESCOPIO", modeled in this document).
Construction recipe (the document's own serialized feature program — sketch geometry with constraints, then the solid features built on it; lengths are millimeters unless a unit is written):

FEATURE [Sketcher::SketchObject] Sketch114
  FullyConstrained = false
  MapMode = 5
  Placement = pos=(0,0,0) rot=(0.57735,0.57735,0.57735;2.0944rad)
  Support = -> [YZ_Plane027]
  sketch-geometry (8):
    g0: LineSegment StartX=-47 StartY=203.208 StartZ=0 EndX=-19 EndY=203.208 EndZ=0
    g1: LineSegment StartX=-19 StartY=203.208 StartZ=0 EndX=-22.5 EndY=189.708 EndZ=0
    g2: LineSegment StartX=-22.5 StartY=189.708 StartZ=0 EndX=22.5 EndY=189.708 EndZ=0
    g3: LineSegment StartX=22.5 StartY=189.708 StartZ=0 EndX=19 EndY=203.208 EndZ=0
    g4: LineSegment StartX=19 StartY=203.208 StartZ=0 EndX=47 EndY=203.208 EndZ=0
    g5: LineSegment StartX=47 StartY=203.208 StartZ=0 EndX=47 EndY=174.471 EndZ=0
    g6: LineSegment StartX=47 StartY=174.471 StartZ=0 EndX=-47 EndY=174.471 EndZ=0
    g7: LineSegment StartX=-47 StartY=174.471 StartZ=0 EndX=-47 EndY=203.208 EndZ=0
  constraints (21):
    c: Horizontal(g0)
    c: Coincident(g0,g1)
    c: Coincident(g1,g2)
    c: Coincident(g2,g3)
    c: Coincident(g3,g4)
    c: Horizontal(g4)
    c: Coincident(g4,g5)
    c: Vertical(g5)
    c: Coincident(g5,g6)
    c: Coincident(g7,g0)
    c: Vertical(g7)
    c: DistanceX(g2,g2) = 45
    c: DistanceY(g1,g1) = 13.5
    c: Horizontal(g3,g0)
    c: DistanceX(g1,g1) = 3.5
    c: DistanceX(g3,g3) = 3.5
    c: Symmetric(g1,g2,g-2)
    c: Symmetric(g6,g5,g-2)
    c: Coincident(g6,g7)
    c: DistanceX(g6,g6) = 94
    c: DistanceX(g6,g6) = 94
FEATURE [PartDesign::Pad] Pad035
  Direction = (1,1,1)
  Length = 77
  Length2 = 100
  Placement = pos=(0,0,0) rot=(0.57735,0.57735,0.57735;2.0944rad)
  Profile = -> Sketch114
  Type = 0
FEATURE [Sketcher::SketchObject] Sketch115
  ExternalGeometry = -> [Pad035]
  FullyConstrained = true
  MapMode = 5
  Placement = pos=(-5.31e-14,8.35e-14,189.708) rot=(0,0,-1;1.5708rad)
  Support = -> [Pad035]
  sketch-geometry (1):
    g0: Circle CenterX=0 CenterY=47 CenterZ=0 NormalX=0 NormalY=0 NormalZ=1 AngleXU=0 Radius=3.1
  constraints (4):
    c: PointOnObject(g0,g-2)
    c: Radius(g0) = 3.1
    c: DistanceY(g-1,g0) = 47
    c: DistanceY(g0,g-3) = 30
FEATURE [PartDesign::Pocket] Pocket071
  BaseFeature = -> Pad035
  Length = 30
  Length2 = 100
  Placement = pos=(0,0,0) rot=(0.57735,0.57735,0.57735;2.0944rad)
  Profile = -> Sketch115
  Type = 0
FEATURE [Sketcher::SketchObject] Sketch116
  ExternalGeometry = -> [Pocket071]
  FullyConstrained = true
  MapMode = 5
  Placement = pos=(-2.07e-14,-47,1.03e-14) rot=(-0.57735,-0.57735,0.57735;4.18879rad)
  Support = -> [Pocket071]
  sketch-geometry (1):
    g0: Circle CenterX=-182.471 CenterY=65 CenterZ=0 NormalX=0 NormalY=0 NormalZ=1 AngleXU=0 Radius=4.3
  constraints (3):
    c: Radius(g0) = 4.3
    c: DistanceY(g-3,g0) = 65
    c: DistanceX(g0,g-3) = 8
FEATURE [PartDesign::Pocket] Pocket072
  BaseFeature = -> Pocket071
  Length = 100
  Length2 = 100
  Placement = pos=(0,0,0) rot=(0.57735,0.57735,0.57735;2.0944rad)
  Profile = -> Sketch116
  Type = 0
FEATURE [PartDesign::Chamfer] Chamfer014
  Angle = 45
  Base = -> Pocket072 [Edge29,Edge1]
  BaseFeature = -> Pocket072
  ChamferType = 0
  FlipDirection = false
  Placement = pos=(0,0,0) rot=(0.57735,0.57735,0.57735;2.0944rad)
  Size = 12
  Size2 = 1
  SupportTransform = false
FEATURE [Sketcher::SketchObject] Sketch117
  ExternalGeometry = -> [Chamfer014]
  FullyConstrained = true
  MapMode = 5
  Placement = pos=(-4e-16,0,0) rot=(0.57735,0.57735,-0.57735;4.18879rad)
  Support = -> [Chamfer014]
  sketch-geometry (6):
    g0: LineSegment StartX=-47 StartY=-174.471 StartZ=0 EndX=47 EndY=-174.471 EndZ=0
    g1: LineSegment StartX=47 StartY=-174.471 StartZ=0 EndX=47 EndY=-191.208 EndZ=0
    g2: LineSegment StartX=47 StartY=-191.208 StartZ=0 EndX=35 EndY=-203.208 EndZ=0
    g3: LineSegment StartX=35 StartY=-203.208 StartZ=0 EndX=-35 EndY=-203.208 EndZ=0
    g4: LineSegment StartX=-35 StartY=-203.208 StartZ=0 EndX=-47 EndY=-191.208 EndZ=0
    g5: LineSegment StartX=-47 StartY=-191.208 StartZ=0 EndX=-47 EndY=-174.471 EndZ=0
  constraints (12):
    c: Coincident(g-4,g0)
    c: Coincident(g0,g-8)
    c: Coincident(g0,g1)
    c: Coincident(g1,g-8)
    c: Coincident(g1,g2)
    c: Coincident(g2,g-7)
    c: Coincident(g2,g3)
    c: Coincident(g3,g-5)
    c: Coincident(g3,g4)
    c: Coincident(g4,g-5)
    c: Coincident(g4,g5)
    c: Coincident(g5,g0)
FEATURE [PartDesign::Pad] Pad036
  BaseFeature = -> Chamfer014
  Direction = (1,1,1)
  Length = 2
  Length2 = 100
  Placement = pos=(0,0,0) rot=(0.57735,0.57735,0.57735;2.0944rad)
  Profile = -> Sketch117
  Type = 0
FEATURE [Sketcher::SketchObject] Sketch118
  ExternalGeometry = -> [Pad036]
  FullyConstrained = true
  MapMode = 5
  Placement = pos=(2.07e-14,47,-1.03e-14) rot=(0.57735,0.57735,0.57735;4.18879rad)
  Support = -> [Pad036]
  sketch-geometry (9):
    g0: LineSegment StartX=174.471 StartY=73 StartZ=0 EndX=204.471 EndY=73 EndZ=0
    g1: LineSegment StartX=204.471 StartY=73 StartZ=0 EndX=204.471 EndY=57 EndZ=0
    g2: LineSegment StartX=204.471 StartY=57 StartZ=0 EndX=174.471 EndY=57 EndZ=0
    g3: LineSegment StartX=174.471 StartY=57 StartZ=0 EndX=174.471 EndY=73 EndZ=0
    g4: GeomPoint X=174.471 Y=65 Z=0
    g5: LineSegment StartX=174.471 StartY=20 StartZ=0 EndX=204.471 EndY=20 EndZ=0
    g6: LineSegment StartX=204.471 StartY=20 StartZ=0 EndX=204.471 EndY=4 EndZ=0
    g7: LineSegment StartX=204.471 StartY=4 StartZ=0 EndX=174.471 EndY=4 EndZ=0
    g8: LineSegment StartX=174.471 StartY=4 StartZ=0 EndX=174.471 EndY=20 EndZ=0
  constraints (27):
    c: Coincident(g0,g1)
    c: Coincident(g1,g2)
    c: Coincident(g2,g3)
    c: Coincident(g3,g0)
    c: Horizontal(g0)
    c: Horizontal(g2)
    c: Vertical(g1)
    c: Vertical(g3)
    c: PointOnObject(g0,g-4)
    c: DistanceY(g3,g3) = 16
    c: Symmetric(g0,g2,g4)
    c: Horizontal(g4,g-3)
    c: DistanceX(g0,g0) = 30
    c: DistanceX(g0,g-3) = 8
    c: Coincident(g5,g6)
    c: Coincident(g6,g7)
    c: Coincident(g7,g8)
    c: Coincident(g8,g5)
    c: Horizontal(g5)
    c: Horizontal(g7)
    c: Vertical(g6)
    c: Vertical(g8)
    c: PointOnObject(g5,g-4)
    c: DistanceX(g5,g5) = 30
    c: DistanceY(g8,g8) = 16
    c: DistanceY(g0,g-4) = 4
    c: DistanceY(g-4,g7) = 4
FEATURE [PartDesign::Pocket] Pocket073
  BaseFeature = -> Pad036
  Length = 8
  Length2 = 100
  Placement = pos=(0,0,0) rot=(0.57735,0.57735,0.57735;2.0944rad)
  Profile = -> Sketch118
  Type = 0
FEATURE [PartDesign::Chamfer] Chamfer023
  Angle = 45
  Base = -> Pocket073 [Edge60,Edge58,Edge69,Edge51,Edge56,Edge54,Edge73,Edge70,Edge50,Edge65,Edge37]
  BaseFeature = -> Pocket073
  ChamferType = 0
  FlipDirection = false
  Placement = pos=(0,0,0) rot=(0.57735,0.57735,0.57735;2.0944rad)
  Size = 0.5
  Size2 = 1
  SupportTransform = false
FEATURE [PartDesign::Body] Body027  label="GRIP TELESCOPIO"
  Group = -> [Sketch114,Pad035,Sketch115,Pocket071,Sketch116,Pocket072,Chamfer014,Sketch117,Pad036,Sketch118,Pocket073,Chamfer023]
  Origin = -> Origin027
  Placement = pos=(-37,0,113) rot=(0,0,1;0rad)
  Tip = -> Chamfer023
COMPONENT P16 — recipe-attached ("RUEDA GRIP", modeled in this document).
Construction recipe (the document's own serialized feature program — sketch geometry with constraints, then the solid features built on it; lengths are millimeters unless a unit is written):

FEATURE [Sketcher::SketchObject] Sketch119
  FullyConstrained = true
  MapMode = 5
  Placement = pos=(0,0,0) rot=(1,0,0;1.5708rad)
  Support = -> [XZ_Plane028]
  sketch-geometry (11):
    g0: LineSegment StartX=43.1 StartY=311.61 StartZ=0 EndX=58.9 EndY=311.61 EndZ=0
    g1: LineSegment StartX=58.9 StartY=311.61 StartZ=0 EndX=58.9 EndY=287.61 EndZ=0
    g2: LineSegment StartX=43.1 StartY=287.61 StartZ=0 EndX=43.1 EndY=311.61 EndZ=0
    g3: Circle CenterX=51.1 CenterY=295.61 CenterZ=0 NormalX=0 NormalY=0 NormalZ=1 AngleXU=0 Radius=4.25
    g4: ArcOfCircle CenterX=51.1 CenterY=295.61 CenterZ=0 NormalX=0 NormalY=0 NormalZ=1 AngleXU=0 Radius=114 StartAngle=3.21183 EndAngle=4.86174
    g5: LineSegment StartX=58.9 StartY=287.61 StartZ=0 EndX=68.0628 EndY=182.879 EndZ=0
    g6: LineSegment StartX=43.1 StartY=287.61 StartZ=0 EndX=5.9 EndY=287.61 EndZ=0
    g7: LineSegment StartX=5.9 StartY=287.61 StartZ=0 EndX=5.9 EndY=311.61 EndZ=0
    g8: LineSegment StartX=5.9 StartY=311.61 StartZ=0 EndX=-9.9 EndY=311.61 EndZ=0
    g9: LineSegment StartX=-9.9 StartY=311.61 StartZ=0 EndX=-9.9 EndY=287.61 EndZ=0
    g10: LineSegment StartX=-9.9 StartY=287.61 StartZ=0 EndX=-62.619 EndY=287.61 EndZ=0
  constraints (34):
    c: Coincident(g0,g1)
    c: Coincident(g2,g0)
    c: Horizontal(g0)
    c: Vertical(g1)
    c: Vertical(g2)
    c: DistanceX(g2,g1) = 15.8
    c: Diameter(g3) = 8.5
    c: DistanceY(g2,g2) = 24
    c: DistanceY(g1,g3) = 8
    c: DistanceX(g2,g3) = 8
    c: DistanceX(g3) = 51.1
    c: DistanceY(g3) = 295.61
    c: Horizontal(g2,g1)
    c: Coincident(g4,g3)
    c: Coincident(g5,g1)
    c: Coincident(g5,g4)
    c: Distance(g3,g4) = 114
    c: Distance(g3,g4) = 114
    c: Angle(g5) = -1.48353
    c: Coincident(g2,g6)
    c: Horizontal(g6)
    c: Coincident(g6,g7)
    c: Vertical(g7)
    c: Coincident(g7,g8)
    c: Horizontal(g8)
    c: Coincident(g8,g9)
    c: Vertical(g9)
    c: Coincident(g9,g10)
    c: Coincident(g10,g4)
    c: Horizontal(g10)
    c: Horizontal(g9,g6)
    c: DistanceX(g8,g8) = 15.8
    c: DistanceY(g9,g9) = 24
    c: DistanceX(g6,g6) = 37.2
FEATURE [PartDesign::Pad] Pad037
  Direction = (1,1,1)
  Length = 8
  Length2 = 100
  Placement = pos=(0,0,0) rot=(1,0,0;1.5708rad)
  Profile = -> Sketch119
  Type = 0
FEATURE [Sketcher::SketchObject] Sketch144
  FullyConstrained = false
  MapMode = 2
  Placement = pos=(0,-2,0) rot=(-1,0,0;1.5708rad)
  Support = -> [Sketch144]
  sketch-geometry (8):
    g0: LineSegment StartX=46.4684 StartY=-270.288 StartZ=0 EndX=51.3899 EndY=-195.713 EndZ=0
    g1: LineSegment StartX=38.2664 StartY=-273.583 StartZ=0 EndX=-45.5854 EndY=-273.501 EndZ=0
    g2: LineSegment StartX=43.65 StartY=-271.06 StartZ=0 EndX=-4.46064 EndY=-213.118 EndZ=0
    g3: LineSegment StartX=46.4684 StartY=-270.288 StartZ=0 EndX=43.65 EndY=-271.06 EndZ=0
    g4: LineSegment StartX=38.2664 StartY=-273.583 StartZ=0 EndX=40.8655 EndY=-272.177 EndZ=0
    g5: LineSegment StartX=40.8655 StartY=-272.177 StartZ=0 EndX=-12.4277 EndY=-219.162 EndZ=0
    g6: ArcOfCircle CenterX=51.9169 CenterY=-295.711 CenterZ=0 NormalX=0 NormalY=0 NormalZ=1 AngleXU=0 Radius=100 StartAngle=2.26979 EndAngle=2.91762
    g7: ArcOfCircle CenterX=51.9169 CenterY=-295.711 CenterZ=0 NormalX=0 NormalY=0 NormalZ=1 AngleXU=0 Radius=100 StartAngle=1.57607 EndAngle=2.16975
  constraints (21):
    c: Coincident(g3,g0)
    c: Coincident(g3,g2)
    c: Coincident(g4,g1)
    c: Coincident(g5,g4)
    c: Coincident(g6,g1)
    c: Coincident(g6,g5)
    c: Coincident(g7,g6)
    c: Coincident(g7,g2)
    c: Coincident(g7,g0)
    c: Radius(g7) = 100
    c: Radius(g6) = 100
    c: Distance(g1,g6) = 26
    c: Distance(g4,g6) = 26
    c: Distance(g2,g6) = 26
    c: Distance(g0,g6) = 26
    c: Distance(g2,g4) = 3
    c: Distance(g4) = 2.955
    c: Distance(g3) = 2.92214
    c: Distance(g5,g2) = 10
    c: Distance(g2,g0) = 58.5
    c: Distance(g5,g1) = 63.6567
FEATURE [PartDesign::Pocket] Pocket089
  BaseFeature = -> Pad037
  Length = 20
  Length2 = 100
  Midplane = true
  Placement = pos=(0,0,0) rot=(1,0,0;1.5708rad)
  Profile = -> Sketch144
  Type = 0
FEATURE [Sketcher::SketchObject] Sketch145
  ExternalGeometry = -> [Pocket089]
  FullyConstrained = false
  MapMode = 5
  Placement = pos=(0,-5e-16,0) rot=(-1,0,0;1.5708rad)
  Support = -> [Pocket089]
  sketch-geometry (4):
    g0: LineSegment StartX=-105.639 StartY=-176.233 StartZ=0 EndX=107.119 EndY=-176.233 EndZ=0
    g1: LineSegment StartX=107.119 StartY=-176.233 StartZ=0 EndX=107.119 EndY=-287.61 EndZ=0
    g2: LineSegment StartX=107.119 StartY=-287.61 StartZ=0 EndX=-105.639 EndY=-287.61 EndZ=0
    g3: LineSegment StartX=-105.639 StartY=-287.61 StartZ=0 EndX=-105.639 EndY=-176.233 EndZ=0
  constraints (9):
    c: Coincident(g0,g1)
    c: Coincident(g1,g2)
    c: Coincident(g2,g3)
    c: Coincident(g3,g0)
    c: Horizontal(g0)
    c: Horizontal(g2)
    c: Vertical(g1)
    c: Vertical(g3)
    c: PointOnObject(g-3,g2)
FEATURE [PartDesign::Pocket] Pocket090
  BaseFeature = -> Pocket089
  Length = 2
  Length2 = 100
  Placement = pos=(0,0,0) rot=(1,0,0;1.5708rad)
  Profile = -> Sketch145
  Type = 0
FEATURE [PartDesign::Chamfer] Chamfer024
  Angle = 45
  Base = -> Pocket090 [Edge13,Edge51]
  BaseFeature = -> Pocket090
  ChamferType = 0
  FlipDirection = false
  Placement = pos=(0,0,0) rot=(1,0,0;1.5708rad)
  Size = 7.9
  Size2 = 1
  SupportTransform = false
FEATURE [Sketcher::SketchObject] Sketch146
  ExternalGeometry = -> [Chamfer024]
  FullyConstrained = true
  MapMode = 5
  Placement = pos=(0,-2,7e-16) rot=(-1,0,0;1.5708rad)
  Support = -> [Chamfer024]
  sketch-geometry (8):
    g0: LineSegment StartX=-61.7716 StartY=-279.61 StartZ=0 EndX=-77.7716 EndY=-279.61 EndZ=0
    g1: LineSegment StartX=-77.7716 StartY=-279.61 StartZ=0 EndX=-77.7716 EndY=-287.61 EndZ=0
    g2: LineSegment StartX=-77.7716 StartY=-287.61 StartZ=0 EndX=-61.7716 EndY=-287.61 EndZ=0
    g3: LineSegment StartX=-61.7716 StartY=-287.61 StartZ=0 EndX=-61.7716 EndY=-279.61 EndZ=0
    g4: LineSegment StartX=60.0628 StartY=-166.879 StartZ=0 EndX=68.0628 EndY=-166.879 EndZ=0
    g5: LineSegment StartX=68.0628 StartY=-166.879 StartZ=0 EndX=68.0628 EndY=-182.879 EndZ=0
    g6: LineSegment StartX=68.0628 StartY=-182.879 StartZ=0 EndX=60.0628 EndY=-182.879 EndZ=0
    g7: LineSegment StartX=60.0628 StartY=-182.879 StartZ=0 EndX=60.0628 EndY=-166.879 EndZ=0
  constraints (23):
    c: Coincident(g0,g1)
    c: Coincident(g1,g2)
    c: Coincident(g2,g3)
    c: Coincident(g3,g0)
    c: Horizontal(g0)
    c: Horizontal(g2)
    c: Vertical(g1)
    c: Vertical(g3)
    c: PointOnObject(g0,g-3)
    c: PointOnObject(g2,g-5)
    c: DistanceY(g1,g1) = 8
    c: DistanceX(g0,g0) = 16
    c: Coincident(g4,g5)
    c: Coincident(g5,g6)
    c: Coincident(g6,g7)
    c: Coincident(g7,g4)
    c: Horizontal(g4)
    c: Horizontal(g6)
    c: Vertical(g5)
    c: Vertical(g7)
    c: Coincident(g5,g-4)
    c: DistanceX(g4,g4) = 8
    c: DistanceY(g5,g5) = 16
FEATURE [PartDesign::Pad] Pad043
  BaseFeature = -> Chamfer024
  Direction = (1,1,1)
  Length = 6
  Length2 = 100
  Placement = pos=(0,0,0) rot=(1,0,0;1.5708rad)
  Profile = -> Sketch146
  Reversed = true
  Type = 0
FEATURE [Sketcher::SketchObject] Sketch147
  ExternalGeometry = -> [Pad043]
  FullyConstrained = false
  MapMode = 5
  Placement = pos=(0,-2,9e-16) rot=(-1,0,0;1.5708rad)
  Support = -> [Pad043]
  sketch-geometry (16):
    g0: LineSegment StartX=59.8525 StartY=-181.714 StartZ=0 EndX=60.0816 EndY=-186.606 EndZ=0
    g1: LineSegment StartX=60.0816 StartY=-186.606 StartZ=0 EndX=55.6004 EndY=-190.801 EndZ=0
    g2: LineSegment StartX=55.6004 StartY=-190.801 StartZ=0 EndX=45.986 EndY=-189.823 EndZ=0
    g3: LineSegment StartX=45.986 StartY=-189.823 StartZ=0 EndX=46.1883 EndY=-187.833 EndZ=0
    g4: LineSegment StartX=46.1883 StartY=-187.833 StartZ=0 EndX=54.8977 EndY=-188.719 EndZ=0
    g5: LineSegment StartX=54.8977 StartY=-188.719 StartZ=0 EndX=58.0406 EndY=-185.777 EndZ=0
    g6: LineSegment StartX=58.0406 StartY=-185.777 StartZ=0 EndX=57.8465 EndY=-181.633 EndZ=0
    g7: LineSegment StartX=57.8465 StartY=-181.633 StartZ=0 EndX=59.8525 EndY=-181.714 EndZ=0
    g8: LineSegment StartX=-62.4277 StartY=-277.477 StartZ=0 EndX=-56.5132 EndY=-277.904 EndZ=0
    g9: LineSegment StartX=-56.5132 StartY=-277.904 StartZ=0 EndX=-52.1059 EndY=-274.289 EndZ=0
    g10: LineSegment StartX=-52.1059 StartY=-274.289 StartZ=0 EndX=-52.1059 EndY=-264.834 EndZ=0
    g11: LineSegment StartX=-52.1059 StartY=-264.834 StartZ=0 EndX=-50.1059 EndY=-264.834 EndZ=0
    g12: LineSegment StartX=-50.1059 StartY=-264.834 StartZ=0 EndX=-50.1059 EndY=-275.235 EndZ=0
    g13: LineSegment StartX=-50.1059 StartY=-275.235 StartZ=0 EndX=-55.8615 EndY=-279.956 EndZ=0
    g14: LineSegment StartX=-55.8615 StartY=-279.956 StartZ=0 EndX=-62.5715 EndY=-279.472 EndZ=0
    g15: LineSegment StartX=-62.5715 StartY=-279.472 StartZ=0 EndX=-62.4277 EndY=-277.477 EndZ=0
  constraints (32):
    c: Coincident(g0,g1)
    c: Coincident(g1,g2)
    c: Coincident(g2,g3)
    c: Coincident(g3,g4)
    c: Coincident(g4,g5)
    c: Coincident(g5,g6)
    c: Coincident(g6,g7)
    c: Coincident(g7,g0)
    c: Parallel(g6,g0)
    c: Parallel(g5,g1)
    c: Parallel(g4,g2)
    c: Perpendicular(g2,g3)
    c: Distance(g4,g2) = 2
    c: Distance(g5,g1) = 2
    c: Distance(g5,g0) = 2
    c: Coincident(g8,g9)
    c: Coincident(g9,g10)
    c: Coincident(g10,g11)
    c: Horizontal(g11)
    c: Coincident(g11,g12)
    c: Coincident(g12,g13)
    c: Coincident(g13,g14)
    c: Coincident(g14,g15)
    c: Coincident(g15,g8)
    c: Parallel(g8,g14)
    c: Perpendicular(g15,g14)
    c: Distance(g8,g14) = 2
    c: Parallel(g9,g13)
    c: Parallel(g10,g12)
    c: Perpendicular(g12,g11)
    c: Distance(g9,g12) = 2
    c: Distance(g8,g13) = 2
FEATURE [PartDesign::Pocket] Pocket091
  BaseFeature = -> Pad043
  Length = 6
  Length2 = 100
  Placement = pos=(0,0,0) rot=(1,0,0;1.5708rad)
  Profile = -> Sketch147
  Type = 0
FEATURE [Sketcher::SketchObject] Sketch148
  ExternalGeometry = -> [Pocket091]
  FullyConstrained = true
  MapMode = 5
  Placement = pos=(0,-2,1.1e-15) rot=(-1,0,0;1.5708rad)
  Support = -> [Pocket091]
  sketch-geometry (2):
    g0: Circle CenterX=-32.566 CenterY=-280.61 CenterZ=0 NormalX=0 NormalY=0 NormalZ=1 AngleXU=0 Radius=5.25
    g1: Circle CenterX=58.1 CenterY=-210.899 CenterZ=0 NormalX=0 NormalY=0 NormalZ=1 AngleXU=0 Radius=5.25
  constraints (9):
    c: Diameter(g1) = 10.5
    c: Diameter(g0) = 10.5
    c: Distance(g1,g-7) = 85
    c: Distance(g0,g-7) = 85
    c: Distance(g1,g-6) = 7.48278
    c: Distance(g1,g-5) = 7.69551
    c: Distance(g0,g-3) = 7
    c: Distance(g0,g-4) = 7.09618
    c: DistanceX(g-7,g1) = 7
FEATURE [PartDesign::Pocket] Pocket092
  BaseFeature = -> Pocket091
  Length = 2
  Length2 = 100
  Placement = pos=(0,0,0) rot=(1,0,0;1.5708rad)
  Profile = -> Sketch148
  Type = 0
FEATURE [PartDesign::Chamfer] Chamfer025
  Angle = 45
  Base = -> Pocket092 [Edge130,Edge129]
  BaseFeature = -> Pocket092
  ChamferType = 0
  FlipDirection = false
  Placement = pos=(0,0,0) rot=(1,0,0;1.5708rad)
  Size = 0.5
  Size2 = 1
  SupportTransform = false
FEATURE [Sketcher::SketchObject] Sketch149
  ExternalGeometry = -> [Chamfer025]
  FullyConstrained = true
  MapMode = 5
  Placement = pos=(0,-2,1.3e-15) rot=(-1,0,0;1.5708rad)
  Support = -> [Chamfer025]
  sketch-geometry (8):
    g0: LineSegment StartX=-56.465 StartY=-282.41 StartZ=0 EndX=-49.215 EndY=-282.41 EndZ=0
    g1: LineSegment StartX=-49.215 StartY=-282.41 StartZ=0 EndX=-49.215 EndY=-284.81 EndZ=0
    g2: LineSegment StartX=-49.215 StartY=-284.81 StartZ=0 EndX=-56.465 EndY=-284.81 EndZ=0
    g3: LineSegment StartX=-56.465 StartY=-284.81 StartZ=0 EndX=-56.465 EndY=-282.41 EndZ=0
    g4: LineSegment StartX=62.6336 StartY=-185.272 StartZ=0 EndX=62.0017 EndY=-192.494 EndZ=0
    g5: LineSegment StartX=62.0017 StartY=-192.494 StartZ=0 EndX=64.3926 EndY=-192.703 EndZ=0
    g6: LineSegment StartX=64.3926 StartY=-192.703 StartZ=0 EndX=65.0245 EndY=-185.481 EndZ=0
    g7: LineSegment StartX=65.0245 StartY=-185.481 StartZ=0 EndX=62.6336 EndY=-185.272 EndZ=0
  constraints (24):
    c: Coincident(g0,g1)
    c: Coincident(g1,g2)
    c: Coincident(g2,g3)
    c: Coincident(g3,g0)
    c: Horizontal(g0)
    c: Horizontal(g2)
    c: Vertical(g1)
    c: Vertical(g3)
    c: Coincident(g4,g5)
    c: Coincident(g5,g6)
    c: Coincident(g6,g7)
    c: Coincident(g7,g4)
    c: Perpendicular(g6,g7)
    c: Perpendicular(g5,g4)
    c: Parallel(g4,g6)
    c: Distance(g7) = 2.4
    c: Distance(g4) = 7.25
    c: DistanceY(g1,g1) = 2.4
    c: DistanceX(g0,g0) = 7.25
    c: Distance(g6,g-3) = 2.8
    c: Parallel(g6,g-3)
    c: Distance(g-3,g6) = 4
    c: Distance(g2,g-4) = 2.8
    c: Distance(g2,g-4) = 6
FEATURE [PartDesign::Pocket] Pocket093
  BaseFeature = -> Chamfer025
  Length = 6
  Length2 = 100
  Placement = pos=(0,0,0) rot=(1,0,0;1.5708rad)
  Profile = -> Sketch149
  Type = 0
FEATURE [Sketcher::SketchObject] Sketch150
  ExternalGeometry = -> [Pocket093]
  FullyConstrained = true
  MapMode = 5
  Placement = pos=(0,2.554e-13,287.61) rot=(0,0,1;3.14159rad)
  Support = -> [Pocket093]
  sketch-geometry (1):
    g0: Circle CenterX=52.8216 CenterY=5 CenterZ=0 NormalX=0 NormalY=0 NormalZ=1 AngleXU=0 Radius=1.6
  constraints (3):
    c: Diameter(g0) = 3.2
    c: Distance(g0,g-3) = 3
    c: DistanceX(g0,g-4) = 8.95
FEATURE [PartDesign::Pocket] Pocket094
  BaseFeature = -> Pocket093
  Length = 11.42
  Length2 = 100
  Placement = pos=(0,0,0) rot=(1,0,0;1.5708rad)
  Profile = -> Sketch150
  Type = 0
FEATURE [Sketcher::SketchObject] Sketch151
  ExternalGeometry = -> [Pocket094]
  FullyConstrained = true
  MapMode = 5
  Placement = pos=(83.4241,7.3e-15,7.29866) rot=(0.67559,0,0.737277;3.14159rad)
  Support = -> [Pocket094]
  sketch-geometry (1):
    g0: Circle CenterX=182.751 CenterY=5 CenterZ=0 NormalX=0 NormalY=0 NormalZ=1 AngleXU=0 Radius=1.6
  constraints (3):
    c: Diameter(g0) = 3.2
    c: Distance(g0,g-4) = 3
    c: DistanceX(g-3,g0) = 6.5
FEATURE [PartDesign::Pocket] Pocket095
  BaseFeature = -> Pocket094
  Length = 10.75
  Length2 = 100
  Placement = pos=(0,0,0) rot=(1,0,0;1.5708rad)
  Profile = -> Sketch151
  Type = 0
FEATURE [PartDesign::Body] Body028  label="RUEDA GRIP"
  Group = -> [Sketch119,Pad037,Sketch144,Pocket089,Sketch145,Pocket090,Chamfer024,Sketch146,Pad043,Sketch147,Pocket091,Sketch148,Pocket092,Chamfer025,Sketch149,Pocket093,Sketch150,Pocket094,Sketch151,Pocket095]
  Origin = -> Origin028
  Placement = pos=(-23,49,0) rot=(0,0,1;0rad)
  Tip = -> Pocket095
COMPONENT P17 — recipe-attached ("BEARING AZIMUT", modeled in this document).
Construction recipe (the document's own serialized feature program — sketch geometry with constraints, then the solid features built on it; lengths are millimeters unless a unit is written):

FEATURE [Sketcher::SketchObject] Sketch122
  FullyConstrained = true
  MapMode = 5
  Support = -> [XY_Plane030]
  sketch-geometry (2):
    g0: Circle CenterX=0 CenterY=0 CenterZ=0 NormalX=0 NormalY=0 NormalZ=1 AngleXU=0 Radius=4
    g1: Circle CenterX=0 CenterY=0 CenterZ=0 NormalX=0 NormalY=0 NormalZ=1 AngleXU=0 Radius=11
  constraints (4):
    c: Coincident(g0,g-1)
    c: Coincident(g1,g0)
    c: Radius(g0) = 4
    c: Radius(g1) = 11
FEATURE [PartDesign::Pad] Pad038
  Direction = (1,1,1)
  Length = 7
  Length2 = 100
  Profile = -> Sketch122
  Type = 0
FEATURE [Sketcher::SketchObject] Sketch124
  FullyConstrained = true
  MapMode = 5
  Placement = pos=(0,0,7) rot=(0,0,1;0rad)
  Support = -> [Pad038]
  sketch-geometry (2):
    g0: Circle CenterX=0 CenterY=0 CenterZ=0 NormalX=0 NormalY=0 NormalZ=1 AngleXU=0 Radius=5.5
    g1: Circle CenterX=0 CenterY=0 CenterZ=0 NormalX=0 NormalY=0 NormalZ=1 AngleXU=0 Radius=5.6
  constraints (4):
    c: Coincident(g0,g-1)
    c: Coincident(g1,g0)
    c: Radius(g0) = 5.5
    c: Radius(g1) = 5.6
FEATURE [PartDesign::Pocket] Pocket074
  BaseFeature = -> Pad038
  Length = 3
  Length2 = 100
  Midplane = true
  Profile = -> Sketch124
  Reversed = true
  Type = 0
FEATURE [Sketcher::SketchObject] Sketch123
  FullyConstrained = true
  MapMode = 5
  Placement = pos=(0,0,0) rot=(1,0,0;3.14159rad)
  Support = -> [Pocket074]
  sketch-geometry (2):
    g0: Circle CenterX=0 CenterY=0 CenterZ=0 NormalX=0 NormalY=0 NormalZ=1 AngleXU=0 Radius=5.5
    g1: Circle CenterX=0 CenterY=0 CenterZ=0 NormalX=0 NormalY=0 NormalZ=1 AngleXU=0 Radius=5.6
  constraints (4):
    c: Coincident(g0,g-1)
    c: Coincident(g1,g0)
    c: Radius(g0) = 5.5
    c: Radius(g1) = 5.6
FEATURE [PartDesign::Pocket] Pocket076
  BaseFeature = -> Pocket074
  Length = 3
  Length2 = 100
  Profile = -> Sketch123
  Type = 0
FEATURE [Sketcher::SketchObject] Sketch120
  FullyConstrained = true
  MapMode = 5
  Placement = pos=(0,0,7) rot=(0,0,1;0rad)
  Support = -> [Pocket076]
  sketch-geometry (2):
    g0: Circle CenterX=0 CenterY=0 CenterZ=0 NormalX=0 NormalY=0 NormalZ=1 AngleXU=0 Radius=9
    g1: Circle CenterX=0 CenterY=0 CenterZ=0 NormalX=0 NormalY=0 NormalZ=1 AngleXU=0 Radius=9.1
  constraints (4):
    c: Coincident(g0,g-1)
    c: Coincident(g1,g0)
    c: Radius(g0) = 9
    c: Radius(g1) = 9.1
FEATURE [PartDesign::Pocket] Pocket077
  BaseFeature = -> Pocket076
  Length = 1
  Length2 = 100
  Profile = -> Sketch120
  Type = 0
FEATURE [Sketcher::SketchObject] Sketch121
  FullyConstrained = true
  MapMode = 5
  Placement = pos=(0,0,0) rot=(1,0,0;3.14159rad)
  Support = -> [Pocket077]
  sketch-geometry (2):
    g0: Circle CenterX=0 CenterY=0 CenterZ=0 NormalX=0 NormalY=0 NormalZ=1 AngleXU=0 Radius=9
    g1: Circle CenterX=0 CenterY=0 CenterZ=0 NormalX=0 NormalY=0 NormalZ=1 AngleXU=0 Radius=9.1
  constraints (4):
    c: Coincident(g0,g-1)
    c: Coincident(g1,g0)
    c: Radius(g0) = 9
    c: Radius(g1) = 9.1
FEATURE [PartDesign::Pocket] Pocket075
  BaseFeature = -> Pocket077
  Length = 1
  Length2 = 100
  Profile = -> Sketch121
  Type = 0
FEATURE [PartDesign::Fillet] Fillet003
  Base = -> Pocket075 [Edge2,Edge3]
  BaseFeature = -> Pocket075
  Radius = 0.2
  SupportTransform = false
FEATURE [PartDesign::Body] Body029  label="BEARING AZIMUT"
  Group = -> [Sketch122,Pad038,Sketch124,Pocket074,Sketch123,Pocket076,Sketch120,Pocket077,Sketch121,Pocket075,Fillet003]
  Origin = -> Origin029
  Placement = pos=(-1.97e-13,-55,296.75) rot=(0.57735,-0.57735,0.57735;2.0944rad)
  Tip = -> Fillet003
COMPONENT P18 — recipe-attached ("cortar aleros", modeled in this document).
Construction recipe (the document's own serialized feature program — sketch geometry with constraints, then the solid features built on it; lengths are millimeters unless a unit is written):

FEATURE [Sketcher::SketchObject] Sketch132
  FullyConstrained = false
  MapMode = 3
  Placement = pos=(-2.8e-15,0,0) rot=(0,0,1;0rad)
  sketch-geometry (2):
    g0: ArcOfCircle CenterX=0 CenterY=-11.2875 CenterZ=0 NormalX=0 NormalY=0 NormalZ=1 AngleXU=0 Radius=30.1865 StartAngle=0.111206 EndAngle=3.03039
    g1: LineSegment StartX=-30 StartY=-7.93752 StartZ=0 EndX=30 EndY=-7.93752 EndZ=0
  constraints (6):
    c: PointOnObject(g0,g-2)
    c: Coincident(g1,g0)
    c: Coincident(g1,g0)
    c: Horizontal(g1)
    c: DistanceY(g0,g0) = 3.35
    c: DistanceX(g0,g0) = 30
FEATURE [PartDesign::Pad] Pad040
  Direction = (1,1,1)
  Length = 7.3
  Length2 = 100
  Placement = pos=(-2.8e-15,0,0) rot=(0,0,1;0rad)
  Profile = -> Sketch132
  Type = 0
FEATURE [PartDesign::Body] Body031  label="cortar aleros"
  Group = -> [Sketch132,Pad040]
  Origin = -> Origin031
  Placement = pos=(0,-1.95,0) rot=(1,0,0;1.5708rad)
  Tip = -> Pad040
COMPONENT P19 — recipe-attached ("cortar bearing", modeled in this document).
Construction recipe (the document's own serialized feature program — sketch geometry with constraints, then the solid features built on it; lengths are millimeters unless a unit is written):

FEATURE [Sketcher::SketchObject] Sketch136
  FullyConstrained = true
  MapMode = 5
  Support = -> [XY_Plane033]
  sketch-geometry (2):
    g0: Circle CenterX=0 CenterY=0 CenterZ=0 NormalX=0 NormalY=0 NormalZ=1 AngleXU=0 Radius=4
    g1: Circle CenterX=0 CenterY=0 CenterZ=0 NormalX=0 NormalY=0 NormalZ=1 AngleXU=0 Radius=11
  constraints (4):
    c: Coincident(g0,g-1)
    c: Coincident(g1,g0)
    c: Radius(g0) = 4
    c: Radius(g1) = 11
FEATURE [PartDesign::Pad] Pad041
  Direction = (1,1,1)
  Length = 7
  Length2 = 100
  Profile = -> Sketch136
  Type = 0
FEATURE [Sketcher::SketchObject] Sketch135
  FullyConstrained = true
  MapMode = 5
  Placement = pos=(0,0,7) rot=(0,0,1;0rad)
  Support = -> [Pad041]
  sketch-geometry (2):
    g0: Circle CenterX=0 CenterY=0 CenterZ=0 NormalX=0 NormalY=0 NormalZ=1 AngleXU=0 Radius=5.5
    g1: Circle CenterX=0 CenterY=0 CenterZ=0 NormalX=0 NormalY=0 NormalZ=1 AngleXU=0 Radius=5.6
  constraints (4):
    c: Coincident(g0,g-1)
    c: Coincident(g1,g0)
    c: Radius(g0) = 5.5
    c: Radius(g1) = 5.6
FEATURE [PartDesign::Pocket] Pocket082
  BaseFeature = -> Pad041
  Length = 3
  Length2 = 100
  Midplane = true
  Profile = -> Sketch135
  Reversed = true
  Type = 0
FEATURE [Sketcher::SketchObject] Sketch137
  FullyConstrained = true
  MapMode = 5
  Placement = pos=(0,0,0) rot=(1,0,0;3.14159rad)
  Support = -> [Pocket082]
  sketch-geometry (2):
    g0: Circle CenterX=0 CenterY=0 CenterZ=0 NormalX=0 NormalY=0 NormalZ=1 AngleXU=0 Radius=5.5
    g1: Circle CenterX=0 CenterY=0 CenterZ=0 NormalX=0 NormalY=0 NormalZ=1 AngleXU=0 Radius=5.6
  constraints (4):
    c: Coincident(g0,g-1)
    c: Coincident(g1,g0)
    c: Radius(g0) = 5.5
    c: Radius(g1) = 5.6
FEATURE [PartDesign::Pocket] Pocket085
  BaseFeature = -> Pocket082
  Length = 3
  Length2 = 100
  Profile = -> Sketch137
  Type = 0
FEATURE [Sketcher::SketchObject] Sketch133
  FullyConstrained = true
  MapMode = 5
  Placement = pos=(0,0,7) rot=(0,0,1;0rad)
  Support = -> [Pocket085]
  sketch-geometry (2):
    g0: Circle CenterX=0 CenterY=0 CenterZ=0 NormalX=0 NormalY=0 NormalZ=1 AngleXU=0 Radius=9
    g1: Circle CenterX=0 CenterY=0 CenterZ=0 NormalX=0 NormalY=0 NormalZ=1 AngleXU=0 Radius=9.1
  constraints (4):
    c: Coincident(g0,g-1)
    c: Coincident(g1,g0)
    c: Radius(g0) = 9
    c: Radius(g1) = 9.1
FEATURE [PartDesign::Pocket] Pocket083
  BaseFeature = -> Pocket085
  Length = 1
  Length2 = 100
  Profile = -> Sketch133
  Type = 0
FEATURE [Sketcher::SketchObject] Sketch134
  FullyConstrained = true
  MapMode = 5
  Placement = pos=(0,0,0) rot=(1,0,0;3.14159rad)
  Support = -> [Pocket083]
  sketch-geometry (2):
    g0: Circle CenterX=0 CenterY=0 CenterZ=0 NormalX=0 NormalY=0 NormalZ=1 AngleXU=0 Radius=9
    g1: Circle CenterX=0 CenterY=0 CenterZ=0 NormalX=0 NormalY=0 NormalZ=1 AngleXU=0 Radius=9.1
  constraints (4):
    c: Coincident(g0,g-1)
    c: Coincident(g1,g0)
    c: Radius(g0) = 9
    c: Radius(g1) = 9.1
FEATURE [PartDesign::Pocket] Pocket084
  BaseFeature = -> Pocket083
  Length = 1
  Length2 = 100
  Profile = -> Sketch134
  Type = 0
FEATURE [PartDesign::Fillet] Fillet004
  Base = -> Pocket084 [Edge2,Edge3]
  BaseFeature = -> Pocket084
  Radius = 0.2
  SupportTransform = false
FEATURE [PartDesign::Body] Body032  label="cortar bearing"
  Group = -> [Sketch136,Pad041,Sketch135,Pocket082,Sketch137,Pocket085,Sketch133,Pocket083,Sketch134,Pocket084,Fillet004]
  Origin = -> Origin032
  Placement = pos=(-1.97e-13,-55,296.75) rot=(0.57735,-0.57735,0.57735;2.0944rad)
  Tip = -> Fillet004
COMPONENT P20 — recipe-attached ("GRIP SUPERIOR", modeled in this document).
Construction recipe (the document's own serialized feature program — sketch geometry with constraints, then the solid features built on it; lengths are millimeters unless a unit is written):

FEATURE [Sketcher::SketchObject] Sketch138
  FullyConstrained = false
  MapMode = 5
  Placement = pos=(0,0,0) rot=(1,0,0;1.5708rad)
  Support = -> [XZ_Plane033]
  sketch-geometry (4):
    g0: LineSegment StartX=-12.4138 StartY=0 StartZ=0 EndX=12.4138 EndY=-5.68e-14 EndZ=0
    g1: LineSegment StartX=12.4138 StartY=-5.68e-14 StartZ=0 EndX=18.1576 EndY=22 EndZ=0
    g2: LineSegment StartX=18.1576 StartY=22 StartZ=0 EndX=-18.1576 EndY=22 EndZ=0
    g3: LineSegment StartX=-18.1576 StartY=22 StartZ=0 EndX=-12.4138 EndY=0 EndZ=0
  constraints (8):
    c: Coincident(g0,g1)
    c: Coincident(g1,g2)
    c: Coincident(g2,g3)
    c: Coincident(g3,g0)
    c: Symmetric(g2,g1,g-2)
    c: Symmetric(g0,g0,g-2)
    c: DistanceY(g0) = 0
    c: DistanceY(g0,g2) = 22
FEATURE [PartDesign::Pad] Pad042
  Direction = (1,1,1)
  Length = 13
  Length2 = 100
  Placement = pos=(0,0,0) rot=(1,0,0;1.5708rad)
  Profile = -> Sketch138
  Type = 0
FEATURE [Sketcher::SketchObject] Sketch139
  ExternalGeometry = -> [Pad042]
  FullyConstrained = true
  MapMode = 5
  Placement = pos=(0,0,0) rot=(-1,0,0;1.5708rad)
  Support = -> [Pad042]
  sketch-geometry (1):
    g0: Circle CenterX=0 CenterY=5.68e-14 CenterZ=0 NormalX=0 NormalY=0 NormalZ=1 AngleXU=0 Radius=11
  constraints (3):
    c: PointOnObject(g0,g-3)
    c: Radius(g0) = 11
    c: PointOnObject(g0,g-2)
FEATURE [PartDesign::Pocket] Pocket086
  BaseFeature = -> Pad042
  Length = 11
  Length2 = 100
  Placement = pos=(0,0,0) rot=(1,0,0;1.5708rad)
  Profile = -> Sketch139
  Type = 0
FEATURE [Sketcher::SketchObject] Sketch140
  ExternalGeometry = -> [Pocket086]
  FullyConstrained = true
  MapMode = 5
  Placement = pos=(0,-13,5.7e-15) rot=(1,0,0;1.5708rad)
  Support = -> [Pocket086]
  sketch-geometry (1):
    g0: Circle CenterX=0 CenterY=-2.84e-14 CenterZ=0 NormalX=0 NormalY=0 NormalZ=1 AngleXU=0 Radius=9.1
  constraints (3):
    c: PointOnObject(g0,g-3)
    c: Radius(g0) = 9.1
    c: PointOnObject(g0,g-2)
FEATURE [PartDesign::Pocket] Pocket087
  BaseFeature = -> Pocket086
  Length = 5
  Length2 = 100
  Placement = pos=(0,0,0) rot=(1,0,0;1.5708rad)
  Profile = -> Sketch140
  Type = 0
FEATURE [PartDesign::Boolean] Boolean
  BaseFeature = -> Pocket087
  Group = -> [Body031]
  Type = 1
FEATURE [Sketcher::SketchObject] Sketch141
  ExternalGeometry = -> [Boolean]
  FullyConstrained = true
  MapMode = 5
  Placement = pos=(0,9.7e-15,22) rot=(0,0,1;0rad)
  Support = -> [Boolean]
  sketch-geometry (1):
    g0: Circle CenterX=0 CenterY=-5.5 CenterZ=0 NormalX=0 NormalY=0 NormalZ=1 AngleXU=0 Radius=1.375
  constraints (3):
    c: Diameter(g0) = 2.75
    c: PointOnObject(g0,g-2)
    c: DistanceY(g0,g-1) = 5.5
FEATURE [PartDesign::Pocket] Pocket088
  BaseFeature = -> Boolean
  Length = 5
  Length2 = 100
  Profile = -> Sketch141
  Type = 0
FEATURE [PartDesign::Chamfer] Chamfer021
  Angle = 45
  Base = -> Pocket088 [Edge20,Edge21]
  BaseFeature = -> Pocket088
  ChamferType = 0
  FlipDirection = false
  Size = 5
  Size2 = 1
  SupportTransform = false
FEATURE [PartDesign::Fillet] Fillet005
  Base = -> Chamfer021 [Edge16,Edge20]
  BaseFeature = -> Chamfer021
  Radius = 1
  SupportTransform = false
FEATURE [PartDesign::Body] Body033  label="GRIP SUPERIOR"
  Group = -> [Sketch138,Pad042,Sketch139,Pocket086,Sketch140,Pocket087,Boolean,Sketch141,Pocket088,Chamfer021,Fillet005]
  Origin = -> Origin033
  Tip = -> Fillet005
